FCSTD DOCUMENT  (FreeCAD 1.0R39285 (Git))
Label: ButtonLayout
License: All rights reserved
LicenseURL: https://en.wikipedia.org/wiki/All_rights_reserved
objects: Sketcher::SketchObject×7, TechDraw::DrawSVGTemplate×3, TechDraw::DrawProjGroupItem×3, TechDraw::DrawPage×3, Spreadsheet::Sheet×1, PartDesign::Body×1
note: 15 computed .brp shape members not serialized (recipe doc carries the construction recipe); baked Part::Feature solids carry a one-line shape summary decoded from their .brp

FEATURE [Sketcher::SketchObject] Sketch  label="SketchB4Rotation"
  ArcFitTolerance = 1e-06
  AttachmentSupport = -> [XY_Plane]
  FullyConstrained = true
  MakeInternals = false
  MapMode = 5
  expr: Constraints[108] = Spreadsheet.HolesEdgeStep
  expr: Constraints[112] = Spreadsheet.HolesEdgeStep
  expr: Constraints[113] = Spreadsheet.HolesEdgeStep
  expr: Constraints[120] = -Spreadsheet.ButtonsCenterOffset
  expr: Constraints[121] = Spreadsheet.ButtonsCenterOffset
  expr: Constraints[148] = Spreadsheet.HolesEdgeStep
  expr: Constraints[149] = Spreadsheet.HolesEdgeStep
  expr: Constraints[54] = Spreadsheet.BoxLength
  expr: Constraints[55] = Spreadsheet.BoxWidth
  expr: Constraints[67] = Spreadsheet.HolesEdgeStep
  expr: Constraints[68] = Spreadsheet.HolesEdgeStep
  expr: Constraints[69] = Spreadsheet.BoxLength / 2
  expr: Constraints[70] = Spreadsheet.BoxWidth / 2
  expr: Constraints[73] = Spreadsheet.Button24Outer
  expr: Constraints[75] = Spreadsheet.Button24Outer
  expr: Constraints[86] = Spreadsheet.OLEDLength
  expr: Constraints[87] = Spreadsheet.OLEDWidth
  sketch-geometry (54):
    g0: Circle CenterX=-22 CenterY=-60.3 CenterZ=0 NormalX=0 NormalY=0 NormalZ=1 AngleXU=0 Radius=15
    g1: Circle CenterX=22 CenterY=-60.3 CenterZ=0 NormalX=0 NormalY=0 NormalZ=1 AngleXU=0 Radius=15
    g2: Circle CenterX=37.5 CenterY=-24.5398 CenterZ=0 NormalX=0 NormalY=0 NormalZ=1 AngleXU=0 Radius=12
    g3: Circle CenterX=69.47 CenterY=18.8602 CenterZ=0 NormalX=0 NormalY=0 NormalZ=1 AngleXU=0 Radius=12
    g4: Circle CenterX=66.57 CenterY=-12.5998 CenterZ=0 NormalX=0 NormalY=0 NormalZ=1 AngleXU=0 Radius=12
    g5: Circle CenterX=100.97 CenterY=18.9602 CenterZ=0 NormalX=0 NormalY=0 NormalZ=1 AngleXU=0 Radius=12
    g6: Circle CenterX=131.97 CenterY=14.9602 CenterZ=0 NormalX=0 NormalY=0 NormalZ=1 AngleXU=0 Radius=12
    g7: Circle CenterX=97.92 CenterY=-12.6198 CenterZ=0 NormalX=0 NormalY=0 NormalZ=1 AngleXU=0 Radius=12
    g8: Circle CenterX=129.01 CenterY=-16.3798 CenterZ=0 NormalX=0 NormalY=0 NormalZ=1 AngleXU=0 Radius=12
    g9: Circle CenterX=-37.5 CenterY=-7 CenterZ=0 NormalX=0 NormalY=0 NormalZ=1 AngleXU=0 Radius=12
    g10: Circle CenterX=-65.5 CenterY=6.5 CenterZ=0 NormalX=0 NormalY=0 NormalZ=1 AngleXU=0 Radius=12
    g11: Circle CenterX=-96.5 CenterY=7.5 CenterZ=0 NormalX=0 NormalY=0 NormalZ=1 AngleXU=0 Radius=12
    g12: Circle CenterX=-128 CenterY=83 CenterZ=0 NormalX=0 NormalY=0 NormalZ=1 AngleXU=0 Radius=12
    g13: Circle CenterX=-95 CenterY=83 CenterZ=0 NormalX=0 NormalY=0 NormalZ=1 AngleXU=0 Radius=12
    g14: Circle CenterX=-62 CenterY=83 CenterZ=0 NormalX=0 NormalY=0 NormalZ=1 AngleXU=0 Radius=12
    g15: Circle CenterX=-29 CenterY=83 CenterZ=0 NormalX=0 NormalY=0 NormalZ=1 AngleXU=0 Radius=12
    g16: Circle CenterX=40.47 CenterY=6.50016 CenterZ=0 NormalX=0 NormalY=0 NormalZ=1 AngleXU=0 Radius=12
    g17: LineSegment StartX=114.5 StartY=92.75 StartZ=0 EndX=114.5 EndY=73.25 EndZ=0
    g18: LineSegment StartX=114.5 StartY=73.25 StartZ=0 EndX=141.5 EndY=73.25 EndZ=0
    g19: LineSegment StartX=141.5 StartY=73.25 StartZ=0 EndX=141.5 EndY=92.75 EndZ=0
    g20: LineSegment StartX=141.5 StartY=92.75 StartZ=0 EndX=114.5 EndY=92.75 EndZ=0
    g21: LineSegment StartX=-172 StartY=127 StartZ=0 EndX=-172 EndY=-127 EndZ=0
    g22: LineSegment StartX=-172 StartY=-127 StartZ=0 EndX=172 EndY=-127 EndZ=0
    g23: LineSegment StartX=172 StartY=-127 StartZ=0 EndX=172 EndY=127 EndZ=0
    g24: LineSegment StartX=172 StartY=127 StartZ=0 EndX=-172 EndY=127 EndZ=0
    g25: LineSegment StartX=-162 StartY=117 StartZ=0 EndX=-162 EndY=-117 EndZ=0
    g26: LineSegment StartX=-162 StartY=-117 StartZ=0 EndX=162 EndY=-117 EndZ=0
    g27: LineSegment StartX=162 StartY=-117 StartZ=0 EndX=162 EndY=117 EndZ=0
    g28: LineSegment StartX=162 StartY=117 StartZ=0 EndX=-162 EndY=117 EndZ=0
    g29: Circle CenterX=-152 CenterY=-107 CenterZ=0 NormalX=0 NormalY=0 NormalZ=1 AngleXU=0 Radius=2
    g30: Circle CenterX=40.47 CenterY=6.50016 CenterZ=0 NormalX=0 NormalY=0 NormalZ=1 AngleXU=0 Radius=14
    g31: Circle CenterX=69.47 CenterY=18.8602 CenterZ=0 NormalX=0 NormalY=0 NormalZ=1 AngleXU=0 Radius=14
    g32: Circle CenterX=100.97 CenterY=18.9602 CenterZ=0 NormalX=0 NormalY=0 NormalZ=1 AngleXU=0 Radius=14
    g33: Circle CenterX=131.97 CenterY=14.9602 CenterZ=0 NormalX=0 NormalY=0 NormalZ=1 AngleXU=0 Radius=14
    g34: Circle CenterX=37.5 CenterY=-24.5398 CenterZ=0 NormalX=0 NormalY=0 NormalZ=1 AngleXU=0 Radius=14
    g35: Circle CenterX=66.57 CenterY=-12.5998 CenterZ=0 NormalX=0 NormalY=0 NormalZ=1 AngleXU=0 Radius=14
    g36: Circle CenterX=97.92 CenterY=-12.6198 CenterZ=0 NormalX=0 NormalY=0 NormalZ=1 AngleXU=0 Radius=14
    g37: Circle CenterX=129.01 CenterY=-16.3798 CenterZ=0 NormalX=0 NormalY=0 NormalZ=1 AngleXU=0 Radius=14
    g38: Circle CenterX=-37.5 CenterY=-7 CenterZ=0 NormalX=0 NormalY=0 NormalZ=1 AngleXU=0 Radius=14
    g39: Circle CenterX=-65.5 CenterY=6.5 CenterZ=0 NormalX=0 NormalY=0 NormalZ=1 AngleXU=0 Radius=14
    g40: Circle CenterX=-96.5 CenterY=7.5 CenterZ=0 NormalX=0 NormalY=0 NormalZ=1 AngleXU=0 Radius=14
    g41: Circle CenterX=-128 CenterY=83 CenterZ=0 NormalX=0 NormalY=0 NormalZ=1 AngleXU=0 Radius=14
    g42: Circle CenterX=-152 CenterY=-107 CenterZ=0 NormalX=0 NormalY=0 NormalZ=1 AngleXU=0 Radius=1.5
    g43: Circle CenterX=152 CenterY=-107 CenterZ=0 NormalX=0 NormalY=0 NormalZ=1 AngleXU=0 Radius=2
    g44: Circle CenterX=152 CenterY=-107 CenterZ=0 NormalX=0 NormalY=0 NormalZ=1 AngleXU=0 Radius=1.5
    g45: Circle CenterX=-152 CenterY=107 CenterZ=0 NormalX=0 NormalY=0 NormalZ=1 AngleXU=0 Radius=2
    g46: Circle CenterX=-152 CenterY=107 CenterZ=0 NormalX=0 NormalY=0 NormalZ=1 AngleXU=0 Radius=1.5
    g47: Circle CenterX=-95 CenterY=83 CenterZ=0 NormalX=0 NormalY=0 NormalZ=1 AngleXU=0 Radius=14
    g48: Circle CenterX=-62 CenterY=83 CenterZ=0 NormalX=0 NormalY=0 NormalZ=1 AngleXU=0 Radius=14
    g49: Circle CenterX=44.47 CenterY=37.0002 CenterZ=0 NormalX=0 NormalY=0 NormalZ=1 AngleXU=0 Radius=12
    g50: Circle CenterX=44.47 CenterY=37.0002 CenterZ=0 NormalX=0 NormalY=0 NormalZ=1 AngleXU=0 Radius=14
    g51: Circle CenterX=-29 CenterY=83 CenterZ=0 NormalX=0 NormalY=0 NormalZ=1 AngleXU=0 Radius=14
    g52: Circle CenterX=152 CenterY=107 CenterZ=0 NormalX=0 NormalY=0 NormalZ=1 AngleXU=0 Radius=2
    g53: Circle CenterX=152 CenterY=107 CenterZ=0 NormalX=0 NormalY=0 NormalZ=1 AngleXU=0 Radius=1.5
  constraints (143):
    c: Equal(g2, g3-g16) x14
    c: Diameter(g2) = 24  '24mm Button'
    c: Equal(g0,g1)
    c: Diameter(g0) = 30  '30mm Button'
    c: DistanceX(g2,g16) = 2.97
    c: DistanceX(g16,g3) = 29
    c: DistanceX(g4,g3) = 2.9
    c: DistanceX(g3,g5) = 31.5
    c: DistanceX(g7,g5) = 3.05
    c: DistanceX(g8,g6) = 2.96
    c: DistanceY(g8,g6) = 31.34
    c: DistanceX(g11,g10) = 31
    c: DistanceX(g10,g9) = 28
    c: DistanceX(g5,g6) = 31
    c: DistanceX(g12,g13) = 33
    c: DistanceX(g13,g14) = 33
    c: DistanceX(g14,g15) = 33
    c: DistanceY(g2,g16) = 31.04  'LP-LK-Y'
    c: DistanceY(g4,g3) = 31.46  'MP-MK-Y'
    c: DistanceY(g9,g10) = 13.5
    c: DistanceX(g9,g0) = 15.5
    c: DistanceY(g0,g9) = 53.3
    c: Coincident(g17,g18)
    c: Coincident(g18,g19)
    c: Coincident(g19,g20)
    c: Coincident(g20,g17)
    c: Vertical(g17)
    c: Vertical(g19)
    c: Horizontal(g18)
    c: Horizontal(g20)
    c: Horizontal(g12,g13)
    c: Horizontal(g13,g14)
    c: Horizontal(g14,g15)
    c: Coincident(g21,g22)
    c: Coincident(g22,g23)
    c: Coincident(g23,g24)
    c: Coincident(g24,g21)
    c: Vertical(g21)
    c: Vertical(g23)
    c: Horizontal(g22)
    c: Horizontal(g24)
    c: DistanceX(g24,g24) = 344
    c: DistanceY(g21,g21) = 254
    c: Coincident(g25,g26)
    c: Coincident(g26,g27)
    c: Coincident(g27,g28)
    c: Coincident(g28,g25)
    c: Vertical(g25)
    c: Vertical(g27)
    c: Horizontal(g26)
    c: Horizontal(g28)
    c: DistanceY(g21,g25) = 10
    c: Distance(g25,g21) = 10
    c: Diameter(g29) = 4
    c: Distance(g29,g26) = 10
    c: Distance(g29,g25) = 10
    c: Distance(g-1,g23) = 172
    c: Distance(g-1,g22) = 127
    c: DistanceY(g7,g5) = 31.58  'HP-HK-Y'
    c: Distance(g16,g3) = 31.5241  'LP-MP-Distance'
    c: Diameter(g30) = 28
    c: Coincident(g30,g16)
    c: Diameter(g31) = 28
    c: Coincident(g31,g3)
    c: Diameter(g32) = 28
    c: Coincident(g32,g5)
    c: Diameter(g33) = 28
    c: Coincident(g33,g6)
    c: Diameter(g34) = 28
    c: Coincident(g34,g2)
    c: DistanceY(g16,g3) = 12.36
    c: Diameter(g35) = 28
    c: Coincident(g35,g4)
    c: DistanceX(g20,g20) = 27
    c: DistanceY(g19,g19) = 19.5
    c: Diameter(g36) = 28
    c: Coincident(g36,g7)
    c: Diameter(g37) = 28
    c: Coincident(g8,g37)
    c: Diameter(g38) = 28
    c: Coincident(g9,g38)
    c: Diameter(g39) = 28
    c: Coincident(g10,g39)
    c: Diameter(g40) = 28
    c: Coincident(g11,g40)
    c: Distance(g10,g9) = 31.0846  'D-R-Distance'
    c: Distance(g4,g16) = 32.3422  'LP-MK-Distance'
    c: Distance(g4,g2) = 31.4266  'LK-MK-Distance'
    c: Diameter(g41) = 28
    c: Coincident(g12,g41)
    c: Diameter(g42) = 3
    c: Coincident(g29,g42)
    c: Diameter(g43) = 4
    c: Diameter(g44) = 3
    c: Coincident(g43,g44)
    c: Distance(g44,g26) = 10
    c: Diameter(g45) = 4
    c: Diameter(g46) = 3
    c: Coincident(g45,g46)
    c: Distance(g45,g28) = 10
    c: Distance(g45,g25) = 10
    c: Distance(g25,g24) = 10
    c: Distance(g9,g22) = 120
    c: Diameter(g47) = 28
    c: Coincident(g13,g47)
    c: Diameter(g48) = 28
    c: Coincident(g14,g48)
    c: DistanceX(g-2,g9) = -37.5
    c: DistanceX(g-2,g2) = 37.5
    c: Symmetric(g1,g0,g-2)
    c: Distance(g11,g10) = 31.0161  'L-D-Distance'
    c: DistanceY(g10,g11) = 1
    c: DistanceY(g6,g5) = 4
    c: DistanceY(g10,g16) = 0.00016
    c: Equal(g49,g16)
    c: DistanceY(g16,g49) = 30.5
    c: Diameter(g50) = 28
    c: Coincident(g49,g50)
    c: DistanceX(g16,g49) = 4
    c: Diameter(g51) = 28
    c: Coincident(g15,g51)
    c: DistanceY(g3,g5) = 0.1
    c: Distance(g3,g5) = 31.5002
    c: Distance(g5,g6) = 31.257
    c: Distance(g16,g49) = 30.7612
    c: Distance(g3,g4) = 31.5934
    c: Distance(g5,g7) = 31.7269
    c: Distance(g6,g8) = 31.4795
    c: Distance(g7,g8) = 31.3165
    c: Distance(g4,g7) = 31.35
    c: Distance(g16,g2) = 31.1818
    c: Distance(g49,g3) = 30.8879
    c: Diameter(g52) = 4
    c: Diameter(g53) = 3
    c: Coincident(g52,g53)
    c: Distance(g52,g28) = 10
    c: Distance(g52,g27) = 10
    c: DistanceY(g12,g45) = 24
    c: DistanceX(g45,g12) = 24
    c: DistanceX(g19,g52) = 10.5
    c: DistanceY(g19,g52) = 14.25
    c: Distance(g43,g27) = 10
    c: Distance(g26,g23) = 10
FEATURE [Spreadsheet::Sheet] Spreadsheet
  cells = A1='Name; B1='Value; C1='Comment; A2='BoxLength; B2(BoxLength)==344 mm; A3='BoxWidth; B3(BoxWidth)==254 mm; A4='Button24; B4(Button24)==24 mm; A5='Button24Outer; B5(Button24Outer)==28 mm; A6='Button30; B6(Button30)==30 mm; A7='Button30Outer; B7(Button30Outer)==33 mm; A8='OLEDLength; B8(OLEDLength)==27 mm; A9='OLEDWidth; B9(OLEDWidth)==19.5 mm; A10='ButtonsCenterOffset; B10(ButtonsCenterOffset)==37.5 mm; A11='Button24FlapWidth; B11(Button24FlapWidth)==4.5 mm; C11='Buttons I have are snap-ins, they have clips on sides; A12='Button24FlapLength; B12(Button24FlapLength)==26.5 mm; C12='Total length of the cutout from one side to another - measured by grabbing the flaps with calipers; A13='HolesEdgeStep; B13(HolesEdgeStep)==10 mm; C13='Step from the edge of acrylic to the center of the corner hole; A14='Button30FlapWidth; B14(Button30FlapWidth)==4.75 mm; A15='Button30FlapLength; B15(Button30FlapLength)==32 mm
FEATURE [Sketcher::SketchObject] Sketch001  label="Sketch10DegInwards"
  ArcFitTolerance = 1e-06
  AttachmentSupport = -> [XY_Plane]
  FullyConstrained = false
  MakeInternals = false
  MapMode = 5
  expr: Constraints[120] = Spreadsheet.Button24FlapLength
  expr: Constraints[121] = Spreadsheet.Button24FlapLength
  expr: Constraints[122] = Spreadsheet.Button24FlapLength
  expr: Constraints[123] = Spreadsheet.Button24FlapLength / 2
  expr: Constraints[124] = Spreadsheet.Button24FlapLength / 2
  expr: Constraints[125] = Spreadsheet.Button24FlapLength / 2
  expr: Constraints[126] = Spreadsheet.Button24FlapWidth
  expr: Constraints[127] = Spreadsheet.Button24FlapWidth
  expr: Constraints[128] = Spreadsheet.Button24FlapWidth
  expr: Constraints[129] = Spreadsheet.Button24FlapWidth / 2
  expr: Constraints[130] = Spreadsheet.Button24FlapWidth / 2
  expr: Constraints[131] = Spreadsheet.Button24FlapWidth / 2
  expr: Constraints[22] = Spreadsheet.BoxLength
  expr: Constraints[23] = Spreadsheet.BoxWidth
  expr: Constraints[259] = Spreadsheet.Button24FlapLength
  expr: Constraints[260] = Spreadsheet.Button24FlapLength
  expr: Constraints[261] = Spreadsheet.Button24FlapLength
  expr: Constraints[262] = Spreadsheet.Button24FlapWidth
  expr: Constraints[275] = Spreadsheet.Button24FlapWidth / 2
  expr: Constraints[276] = Spreadsheet.Button24FlapWidth / 2
  expr: Constraints[277] = Spreadsheet.Button24FlapWidth / 2
  expr: Constraints[278] = Spreadsheet.Button24FlapWidth / 2
  expr: Constraints[279] = Spreadsheet.Button24FlapWidth / 2
  expr: Constraints[280] = Spreadsheet.Button24FlapWidth / 2
  expr: Constraints[281] = Spreadsheet.Button24FlapWidth / 2
  expr: Constraints[282] = Spreadsheet.Button24FlapWidth / 2
  expr: Constraints[283] = Spreadsheet.Button24FlapWidth / 2
  expr: Constraints[284] = Spreadsheet.Button24FlapWidth / 2
  expr: Constraints[285] = Spreadsheet.Button24FlapWidth / 2
  expr: Constraints[286] = Spreadsheet.Button24FlapWidth / 2
  expr: Constraints[287] = Spreadsheet.Button24FlapWidth / 2
  expr: Constraints[288] = Spreadsheet.Button24FlapLength / 2
  expr: Constraints[289] = Spreadsheet.Button24FlapLength
  expr: Constraints[290] = Spreadsheet.Button24FlapLength / 2
  expr: Constraints[291] = Spreadsheet.Button24FlapLength / 2
  expr: Constraints[292] = Spreadsheet.Button24FlapLength / 2
  expr: Constraints[293] = Spreadsheet.Button24FlapLength / 2
  expr: Constraints[294] = Spreadsheet.Button24FlapLength / 2
  expr: Constraints[295] = Spreadsheet.Button24FlapLength / 2
  expr: Constraints[296] = Spreadsheet.Button24FlapLength / 2
  expr: Constraints[297] = Spreadsheet.Button24FlapLength / 2
  expr: Constraints[298] = Spreadsheet.Button24FlapLength / 2
  expr: Constraints[299] = Spreadsheet.Button24FlapLength / 2
  expr: Constraints[300] = Spreadsheet.Button24FlapLength / 2
  expr: Constraints[301] = Spreadsheet.Button24FlapLength / 2
  expr: Constraints[35] = Spreadsheet.HolesEdgeStep
  expr: Constraints[36] = Spreadsheet.HolesEdgeStep
  expr: Constraints[37] = Spreadsheet.BoxLength / 2
  expr: Constraints[38] = Spreadsheet.BoxWidth / 2
  expr: Constraints[39] = Spreadsheet.OLEDLength
  expr: Constraints[409] = Spreadsheet.Button30
  expr: Constraints[40] = Spreadsheet.OLEDWidth
  expr: Constraints[427] = Spreadsheet.Button30FlapLength
  expr: Constraints[428] = Spreadsheet.Button30FlapLength / 2
  expr: Constraints[429] = Spreadsheet.Button30FlapLength / 2
  expr: Constraints[430] = Spreadsheet.Button30FlapWidth
  expr: Constraints[431] = Spreadsheet.Button30FlapWidth / 2
  expr: Constraints[432] = Spreadsheet.Button30FlapWidth / 2
  expr: Constraints[43] = Spreadsheet.HolesEdgeStep
  expr: Constraints[44] = Spreadsheet.HolesEdgeStep
  expr: Constraints[48] = Spreadsheet.HolesEdgeStep
  expr: Constraints[49] = Spreadsheet.HolesEdgeStep
  expr: Constraints[50] = Spreadsheet.HolesEdgeStep
  expr: Constraints[63] = Spreadsheet.ButtonsCenterOffset
  expr: Constraints[81] = -Spreadsheet.ButtonsCenterOffset
  sketch-geometry (160):
    g0: ArcOfCircle CenterX=-128 CenterY=83 CenterZ=0 NormalX=0 NormalY=0 NormalZ=1 AngleXU=0 Radius=12 StartAngle=3.33021 EndAngle=6.09457
    g1: ArcOfCircle CenterX=-95 CenterY=83 CenterZ=0 NormalX=0 NormalY=0 NormalZ=1 AngleXU=0 Radius=12 StartAngle=3.33021 EndAngle=6.09457
    g2: ArcOfCircle CenterX=-62 CenterY=83 CenterZ=0 NormalX=0 NormalY=0 NormalZ=1 AngleXU=0 Radius=12 StartAngle=3.33021 EndAngle=6.09457
    g3: ArcOfCircle CenterX=-29 CenterY=83 CenterZ=0 NormalX=0 NormalY=0 NormalZ=1 AngleXU=0 Radius=12 StartAngle=3.33021 EndAngle=6.09457
    g4: LineSegment StartX=114.5 StartY=92.75 StartZ=0 EndX=114.5 EndY=73.25 EndZ=0
    g5: LineSegment StartX=114.5 StartY=73.25 StartZ=0 EndX=141.5 EndY=73.25 EndZ=0
    g6: LineSegment StartX=141.5 StartY=73.25 StartZ=0 EndX=141.5 EndY=92.75 EndZ=0
    g7: LineSegment StartX=141.5 StartY=92.75 StartZ=0 EndX=114.5 EndY=92.75 EndZ=0
    g8: LineSegment StartX=-172 StartY=127 StartZ=0 EndX=-172 EndY=-127 EndZ=0
    g9: LineSegment StartX=-172 StartY=-127 StartZ=0 EndX=172 EndY=-127 EndZ=0
    g10: LineSegment StartX=172 StartY=-127 StartZ=0 EndX=172 EndY=127 EndZ=0
    g11: LineSegment StartX=172 StartY=127 StartZ=0 EndX=-172 EndY=127 EndZ=0
    g12: LineSegment StartX=-162 StartY=117 StartZ=0 EndX=-162 EndY=-117 EndZ=0
    g13: LineSegment StartX=-162 StartY=-117 StartZ=0 EndX=162 EndY=-117 EndZ=0
    g14: LineSegment StartX=162 StartY=-117 StartZ=0 EndX=162 EndY=117 EndZ=0
    g15: LineSegment StartX=162 StartY=117 StartZ=0 EndX=-162 EndY=117 EndZ=0
    g16: Circle CenterX=-152 CenterY=-107 CenterZ=0 NormalX=0 NormalY=0 NormalZ=1 AngleXU=0 Radius=2
    g17: Circle CenterX=152 CenterY=-107 CenterZ=0 NormalX=0 NormalY=0 NormalZ=1 AngleXU=0 Radius=2
    g18: Circle CenterX=-152 CenterY=107 CenterZ=0 NormalX=0 NormalY=0 NormalZ=1 AngleXU=0 Radius=2
    g19: Circle CenterX=152 CenterY=107 CenterZ=0 NormalX=0 NormalY=0 NormalZ=1 AngleXU=0 Radius=2
    g20: ArcOfCircle CenterX=-37.5 CenterY=-5.11795 CenterZ=0 NormalX=0 NormalY=0 NormalZ=1 AngleXU=0 Radius=12 StartAngle=3.33021 EndAngle=6.09457
    g21: ArcOfCircle CenterX=-62.72 CenterY=13.0402 CenterZ=0 NormalX=0 NormalY=0 NormalZ=1 AngleXU=0 Radius=12 StartAngle=3.33021 EndAngle=6.09457
    g22: ArcOfCircle CenterX=-93.08 CenterY=19.4093 CenterZ=0 NormalX=0 NormalY=0 NormalZ=1 AngleXU=0 Radius=12 StartAngle=3.33021 EndAngle=6.09457
    g23: ArcOfCircle CenterX=37.5 CenterY=-22.3921 CenterZ=0 NormalX=0 NormalY=0 NormalZ=1 AngleXU=0 Radius=12 StartAngle=3.33021 EndAngle=6.09457
    g24: ArcOfCircle CenterX=61.45 CenterY=25.8987 CenterZ=0 NormalX=0 NormalY=0 NormalZ=1 AngleXU=0 Radius=12 StartAngle=3.33021 EndAngle=6.09457
    g25: ArcOfCircle CenterX=64.06 CenterY=-5.58705 CenterZ=0 NormalX=0 NormalY=0 NormalZ=1 AngleXU=0 Radius=12 StartAngle=3.33021 EndAngle=6.09457
    g26: ArcOfCircle CenterX=92.46 CenterY=31.4654 CenterZ=0 NormalX=0 NormalY=0 NormalZ=1 AngleXU=0 Radius=12 StartAngle=3.33021 EndAngle=6.09457
    g27: ArcOfCircle CenterX=123.68 CenterY=32.9074 CenterZ=0 NormalX=0 NormalY=0 NormalZ=1 AngleXU=0 Radius=12 StartAngle=3.33021 EndAngle=6.09457
    g28: ArcOfCircle CenterX=94.93 CenterY=-0.164634 CenterZ=0 NormalX=0 NormalY=0 NormalZ=1 AngleXU=0 Radius=12 StartAngle=3.33021 EndAngle=6.09457
    g29: ArcOfCircle CenterX=126.2 CenterY=1.52943 CenterZ=0 NormalX=0 NormalY=0 NormalZ=1 AngleXU=0 Radius=12 StartAngle=3.33021 EndAngle=6.09457
    g30: ArcOfCircle CenterX=35.04 CenterY=8.69222 CenterZ=0 NormalX=0 NormalY=0 NormalZ=1 AngleXU=0 Radius=12 StartAngle=0.188616 EndAngle=2.95298
    g31: ArcOfCircle CenterX=33.68 CenterY=39.4235 CenterZ=0 NormalX=0 NormalY=0 NormalZ=1 AngleXU=0 Radius=12 StartAngle=3.33021 EndAngle=6.09457
    g32: LineSegment StartX=-106.33 StartY=21.6593 StartZ=0 EndX=-106.33 EndY=17.1593 EndZ=0
    g33: LineSegment StartX=-106.33 StartY=17.1593 StartZ=0 EndX=-104.867 EndY=17.1593 EndZ=0
    g34: LineSegment StartX=-79.83 StartY=17.1593 StartZ=0 EndX=-79.83 EndY=21.6593 EndZ=0
    g35: LineSegment StartX=-79.83 StartY=21.6593 StartZ=0 EndX=-81.2928 EndY=21.6593 EndZ=0
    g36: LineSegment StartX=-75.97 StartY=15.2902 StartZ=0 EndX=-75.97 EndY=10.7902 EndZ=0
    g37: LineSegment StartX=-75.97 StartY=10.7902 StartZ=0 EndX=-74.5072 EndY=10.7902 EndZ=0
    g38: LineSegment StartX=-49.47 StartY=10.7902 StartZ=0 EndX=-49.47 EndY=15.2902 EndZ=0
    g39: LineSegment StartX=-49.47 StartY=15.2902 StartZ=0 EndX=-50.9328 EndY=15.2902 EndZ=0
    g40: LineSegment StartX=-50.75 StartY=-2.86795 StartZ=0 EndX=-50.75 EndY=-7.36795 EndZ=0
    g41: LineSegment StartX=-50.75 StartY=-7.36795 StartZ=0 EndX=-49.2872 EndY=-7.36795 EndZ=0
    g42: LineSegment StartX=-24.25 StartY=-7.36795 StartZ=0 EndX=-24.25 EndY=-2.86795 EndZ=0
    g43: LineSegment StartX=-24.25 StartY=-2.86795 StartZ=0 EndX=-25.7128 EndY=-2.86795 EndZ=0
    g44: LineSegment StartX=-104.867 StartY=21.6593 StartZ=0 EndX=-106.33 EndY=21.6593 EndZ=0
    g45: LineSegment StartX=-81.2928 StartY=17.1593 StartZ=0 EndX=-79.83 EndY=17.1593 EndZ=0
    g46: ArcOfCircle CenterX=-93.08 CenterY=19.4093 CenterZ=0 NormalX=0 NormalY=0 NormalZ=1 AngleXU=0 Radius=12 StartAngle=0.188616 EndAngle=2.95298
    g47: ArcOfCircle CenterX=-62.72 CenterY=13.0402 CenterZ=0 NormalX=0 NormalY=0 NormalZ=1 AngleXU=0 Radius=12 StartAngle=0.188616 EndAngle=2.95298
    g48: LineSegment StartX=-74.5072 StartY=15.2902 StartZ=0 EndX=-75.97 EndY=15.2902 EndZ=0
    g49: LineSegment StartX=-50.9328 StartY=10.7902 StartZ=0 EndX=-49.47 EndY=10.7902 EndZ=0
    g50: LineSegment StartX=-49.2872 StartY=-2.86795 StartZ=0 EndX=-50.75 EndY=-2.86795 EndZ=0
    g51: LineSegment StartX=-25.7128 StartY=-7.36795 StartZ=0 EndX=-24.25 EndY=-7.36795 EndZ=0
    g52: ArcOfCircle CenterX=-37.5 CenterY=-5.11795 CenterZ=0 NormalX=0 NormalY=0 NormalZ=1 AngleXU=0 Radius=12 StartAngle=0.188616 EndAngle=2.95298
    g53: LineSegment StartX=20.43 StartY=41.6735 StartZ=0 EndX=20.43 EndY=37.1735 EndZ=0
    g54: LineSegment StartX=20.43 StartY=37.1735 StartZ=0 EndX=21.8928 EndY=37.1735 EndZ=0
    g55: LineSegment StartX=46.93 StartY=37.1735 StartZ=0 EndX=46.93 EndY=41.6735 EndZ=0
    g56: LineSegment StartX=46.93 StartY=41.6735 StartZ=0 EndX=45.4672 EndY=41.6735 EndZ=0
    g57: LineSegment StartX=21.79 StartY=10.9422 StartZ=0 EndX=21.79 EndY=6.44222 EndZ=0
    g58: LineSegment StartX=21.79 StartY=6.44222 StartZ=0 EndX=23.2528 EndY=6.44222 EndZ=0
    g59: LineSegment StartX=48.29 StartY=6.44222 StartZ=0 EndX=48.29 EndY=10.9422 EndZ=0
    g60: LineSegment StartX=48.29 StartY=10.9422 StartZ=0 EndX=46.8272 EndY=10.9422 EndZ=0
    g61: LineSegment StartX=24.25 StartY=-20.1421 StartZ=0 EndX=24.25 EndY=-24.6421 EndZ=0
    g62: LineSegment StartX=24.25 StartY=-24.6421 StartZ=0 EndX=25.7128 EndY=-24.6421 EndZ=0
    g63: LineSegment StartX=50.75 StartY=-24.6421 StartZ=0 EndX=50.75 EndY=-20.1421 EndZ=0
    g64: LineSegment StartX=50.75 StartY=-20.1421 StartZ=0 EndX=49.2872 EndY=-20.1421 EndZ=0
    g65: LineSegment StartX=50.81 StartY=-3.33705 StartZ=0 EndX=50.81 EndY=-7.83705 EndZ=0
    g66: LineSegment StartX=50.81 StartY=-7.83705 StartZ=0 EndX=52.2728 EndY=-7.83705 EndZ=0
    g67: LineSegment StartX=77.31 StartY=-7.83705 StartZ=0 EndX=77.31 EndY=-3.33705 EndZ=0
    g68: LineSegment StartX=77.31 StartY=-3.33705 StartZ=0 EndX=75.8472 EndY=-3.33705 EndZ=0
    g69: LineSegment StartX=48.2 StartY=28.1487 StartZ=0 EndX=48.2 EndY=23.6487 EndZ=0
    g70: LineSegment StartX=48.2 StartY=23.6487 StartZ=0 EndX=49.6628 EndY=23.6487 EndZ=0
    g71: LineSegment StartX=74.7 StartY=23.6487 StartZ=0 EndX=74.7 EndY=28.1487 EndZ=0
    g72: LineSegment StartX=74.7 StartY=28.1487 StartZ=0 EndX=73.2372 EndY=28.1487 EndZ=0
    g73: LineSegment StartX=79.21 StartY=33.7154 StartZ=0 EndX=79.21 EndY=29.2154 EndZ=0
    g74: LineSegment StartX=79.21 StartY=29.2154 StartZ=0 EndX=80.6728 EndY=29.2154 EndZ=0
    g75: LineSegment StartX=105.71 StartY=29.2154 StartZ=0 EndX=105.71 EndY=33.7154 EndZ=0
    g76: LineSegment StartX=105.71 StartY=33.7154 StartZ=0 EndX=104.247 EndY=33.7154 EndZ=0
    g77: LineSegment StartX=110.43 StartY=35.1574 StartZ=0 EndX=110.43 EndY=30.6574 EndZ=0
    g78: LineSegment StartX=110.43 StartY=30.6574 StartZ=0 EndX=111.893 EndY=30.6574 EndZ=0
    g79: LineSegment StartX=136.93 StartY=30.6574 StartZ=0 EndX=136.93 EndY=35.1574 EndZ=0
    g80: LineSegment StartX=136.93 StartY=35.1574 StartZ=0 EndX=135.467 EndY=35.1574 EndZ=0
    g81: LineSegment StartX=81.68 StartY=2.08537 StartZ=0 EndX=81.68 EndY=-2.41463 EndZ=0
    g82: LineSegment StartX=81.68 StartY=-2.41463 StartZ=0 EndX=83.1428 EndY=-2.41463 EndZ=0
    g83: LineSegment StartX=108.18 StartY=-2.41463 StartZ=0 EndX=108.18 EndY=2.08537 EndZ=0
    g84: LineSegment StartX=108.18 StartY=2.08537 StartZ=0 EndX=106.717 EndY=2.08537 EndZ=0
    g85: LineSegment StartX=112.95 StartY=3.77943 StartZ=0 EndX=112.95 EndY=-0.720574 EndZ=0
    g86: LineSegment StartX=112.95 StartY=-0.720574 StartZ=0 EndX=114.413 EndY=-0.720574 EndZ=0
    g87: LineSegment StartX=139.45 StartY=-0.720574 StartZ=0 EndX=139.45 EndY=3.77943 EndZ=0
    g88: LineSegment StartX=139.45 StartY=3.77943 StartZ=0 EndX=137.987 EndY=3.77943 EndZ=0
    g89: LineSegment StartX=-141.25 StartY=85.25 StartZ=0 EndX=-141.25 EndY=80.75 EndZ=0
    g90: LineSegment StartX=-141.25 StartY=80.75 StartZ=0 EndX=-139.787 EndY=80.75 EndZ=0
    g91: LineSegment StartX=-114.75 StartY=80.75 StartZ=0 EndX=-114.75 EndY=85.25 EndZ=0
    g92: LineSegment StartX=-114.75 StartY=85.25 StartZ=0 EndX=-116.213 EndY=85.25 EndZ=0
    g93: LineSegment StartX=-108.25 StartY=85.25 StartZ=0 EndX=-108.25 EndY=80.75 EndZ=0
    g94: LineSegment StartX=-108.25 StartY=80.75 StartZ=0 EndX=-106.787 EndY=80.75 EndZ=0
    g95: LineSegment StartX=-81.75 StartY=80.75 StartZ=0 EndX=-81.75 EndY=85.25 EndZ=0
    g96: LineSegment StartX=-81.75 StartY=85.25 StartZ=0 EndX=-83.2128 EndY=85.25 EndZ=0
    g97: LineSegment StartX=-75.25 StartY=85.25 StartZ=0 EndX=-75.25 EndY=80.75 EndZ=0
    g98: LineSegment StartX=-75.25 StartY=80.75 StartZ=0 EndX=-73.7872 EndY=80.75 EndZ=0
    g99: LineSegment StartX=-48.75 StartY=80.75 StartZ=0 EndX=-48.75 EndY=85.25 EndZ=0
    g100: LineSegment StartX=-48.75 StartY=85.25 StartZ=0 EndX=-50.2128 EndY=85.25 EndZ=0
    g101: LineSegment StartX=-42.25 StartY=85.25 StartZ=0 EndX=-42.25 EndY=80.75 EndZ=0
    g102: LineSegment StartX=-42.25 StartY=80.75 StartZ=0 EndX=-40.7872 EndY=80.75 EndZ=0
    g103: LineSegment StartX=-15.75 StartY=80.75 StartZ=0 EndX=-15.75 EndY=85.25 EndZ=0
    g104: LineSegment StartX=-15.75 StartY=85.25 StartZ=0 EndX=-17.2128 EndY=85.25 EndZ=0
    g105: LineSegment StartX=-139.787 StartY=85.25 StartZ=0 EndX=-141.25 EndY=85.25 EndZ=0
    g106: LineSegment StartX=-116.213 StartY=80.75 StartZ=0 EndX=-114.75 EndY=80.75 EndZ=0
    g107: ArcOfCircle CenterX=-128 CenterY=83 CenterZ=0 NormalX=0 NormalY=0 NormalZ=1 AngleXU=0 Radius=12 StartAngle=0.188616 EndAngle=2.95298
    g108: LineSegment StartX=-106.787 StartY=85.25 StartZ=0 EndX=-108.25 EndY=85.25 EndZ=0
    g109: LineSegment StartX=-83.2128 StartY=80.75 StartZ=0 EndX=-81.75 EndY=80.75 EndZ=0
    g110: ArcOfCircle CenterX=-95 CenterY=83 CenterZ=0 NormalX=0 NormalY=0 NormalZ=1 AngleXU=0 Radius=12 StartAngle=0.188616 EndAngle=2.95298
    g111: LineSegment StartX=-73.7872 StartY=85.25 StartZ=0 EndX=-75.25 EndY=85.25 EndZ=0
    g112: LineSegment StartX=-50.2128 StartY=80.75 StartZ=0 EndX=-48.75 EndY=80.75 EndZ=0
    g113: ArcOfCircle CenterX=-62 CenterY=83 CenterZ=0 NormalX=0 NormalY=0 NormalZ=1 AngleXU=0 Radius=12 StartAngle=0.188616 EndAngle=2.95298
    g114: LineSegment StartX=-40.7872 StartY=85.25 StartZ=0 EndX=-42.25 EndY=85.25 EndZ=0
    g115: LineSegment StartX=-17.2128 StartY=80.75 StartZ=0 EndX=-15.75 EndY=80.75 EndZ=0
    g116: ArcOfCircle CenterX=-29 CenterY=83 CenterZ=0 NormalX=0 NormalY=0 NormalZ=1 AngleXU=0 Radius=12 StartAngle=0.188616 EndAngle=2.95298
    g117: ArcOfCircle CenterX=33.68 CenterY=39.4235 CenterZ=0 NormalX=0 NormalY=0 NormalZ=1 AngleXU=0 Radius=12 StartAngle=0.188616 EndAngle=2.95298
    g118: LineSegment StartX=21.8928 StartY=41.6735 StartZ=0 EndX=20.43 EndY=41.6735 EndZ=0
    g119: LineSegment StartX=45.4672 StartY=37.1735 StartZ=0 EndX=46.93 EndY=37.1735 EndZ=0
    g120: LineSegment StartX=49.6628 StartY=28.1487 StartZ=0 EndX=48.2 EndY=28.1487 EndZ=0
    g121: LineSegment StartX=73.2372 StartY=23.6487 StartZ=0 EndX=74.7 EndY=23.6487 EndZ=0
    g122: ArcOfCircle CenterX=61.45 CenterY=25.8987 CenterZ=0 NormalX=0 NormalY=0 NormalZ=1 AngleXU=0 Radius=12 StartAngle=0.188616 EndAngle=2.95298
    g123: LineSegment StartX=80.6728 StartY=33.7154 StartZ=0 EndX=79.21 EndY=33.7154 EndZ=0
    g124: LineSegment StartX=104.247 StartY=29.2154 StartZ=0 EndX=105.71 EndY=29.2154 EndZ=0
    g125: ArcOfCircle CenterX=92.46 CenterY=31.4654 CenterZ=0 NormalX=0 NormalY=0 NormalZ=1 AngleXU=0 Radius=12 StartAngle=0.188616 EndAngle=2.95298
    g126: LineSegment StartX=111.893 StartY=35.1574 StartZ=0 EndX=110.43 EndY=35.1574 EndZ=0
    g127: LineSegment StartX=135.467 StartY=30.6574 StartZ=0 EndX=136.93 EndY=30.6574 EndZ=0
    g128: ArcOfCircle CenterX=123.68 CenterY=32.9074 CenterZ=0 NormalX=0 NormalY=0 NormalZ=1 AngleXU=0 Radius=12 StartAngle=0.188616 EndAngle=2.95298
    g129: ArcOfCircle CenterX=35.04 CenterY=8.69222 CenterZ=0 NormalX=0 NormalY=0 NormalZ=1 AngleXU=0 Radius=12 StartAngle=3.33021 EndAngle=6.09457
    g130: LineSegment StartX=23.2528 StartY=10.9422 StartZ=0 EndX=21.79 EndY=10.9422 EndZ=0
    g131: LineSegment StartX=46.8272 StartY=6.44222 StartZ=0 EndX=48.29 EndY=6.44222 EndZ=0
    g132: LineSegment StartX=25.7128 StartY=-20.1421 StartZ=0 EndX=24.25 EndY=-20.1421 EndZ=0
    g133: LineSegment StartX=49.2872 StartY=-24.6421 StartZ=0 EndX=50.75 EndY=-24.6421 EndZ=0
    g134: ArcOfCircle CenterX=37.5 CenterY=-22.3921 CenterZ=0 NormalX=0 NormalY=0 NormalZ=1 AngleXU=0 Radius=12 StartAngle=0.188616 EndAngle=2.95298
    g135: ArcOfCircle CenterX=64.06 CenterY=-5.58705 CenterZ=0 NormalX=0 NormalY=0 NormalZ=1 AngleXU=0 Radius=12 StartAngle=0.188616 EndAngle=2.95298
    g136: LineSegment StartX=52.2728 StartY=-3.33705 StartZ=0 EndX=50.81 EndY=-3.33705 EndZ=0
    g137: LineSegment StartX=75.8472 StartY=-7.83705 StartZ=0 EndX=77.31 EndY=-7.83705 EndZ=0
    g138: LineSegment StartX=83.1428 StartY=2.08537 StartZ=0 EndX=81.68 EndY=2.08537 EndZ=0
    g139: ArcOfCircle CenterX=94.93 CenterY=-0.164634 CenterZ=0 NormalX=0 NormalY=0 NormalZ=1 AngleXU=0 Radius=12 StartAngle=0.188616 EndAngle=2.95298
    g140: LineSegment StartX=106.717 StartY=-2.41463 StartZ=0 EndX=108.18 EndY=-2.41463 EndZ=0
    g141: LineSegment StartX=114.413 StartY=3.77943 StartZ=0 EndX=112.95 EndY=3.77943 EndZ=0
    g142: LineSegment StartX=137.987 StartY=-0.720574 StartZ=0 EndX=139.45 EndY=-0.720574 EndZ=0
    g143: ArcOfCircle CenterX=126.2 CenterY=1.52943 CenterZ=0 NormalX=0 NormalY=0 NormalZ=1 AngleXU=0 Radius=12 StartAngle=0.188616 EndAngle=2.95298
    g144: ArcOfCircle CenterX=28.44 CenterY=-60.3 CenterZ=0 NormalX=0 NormalY=0 NormalZ=1 AngleXU=0 Radius=15 StartAngle=3.3006 EndAngle=6.12418
    g145: ArcOfCircle CenterX=-31.49 CenterY=-60.3 CenterZ=0 NormalX=0 NormalY=0 NormalZ=1 AngleXU=0 Radius=15 StartAngle=3.3006 EndAngle=6.12418
    g146: LineSegment StartX=-47.49 StartY=-57.925 StartZ=0 EndX=-47.49 EndY=-62.675 EndZ=0
    g147: LineSegment StartX=-47.49 StartY=-62.675 StartZ=0 EndX=-46.3008 EndY=-62.675 EndZ=0
    g148: LineSegment StartX=-15.49 StartY=-62.675 StartZ=0 EndX=-15.49 EndY=-57.925 EndZ=0
    g149: LineSegment StartX=-15.49 StartY=-57.925 StartZ=0 EndX=-16.6792 EndY=-57.925 EndZ=0
    g150: LineSegment StartX=12.44 StartY=-57.925 StartZ=0 EndX=12.44 EndY=-62.675 EndZ=0
    g151: LineSegment StartX=12.44 StartY=-62.675 StartZ=0 EndX=13.6292 EndY=-62.675 EndZ=0
    g152: LineSegment StartX=44.44 StartY=-62.675 StartZ=0 EndX=44.44 EndY=-57.925 EndZ=0
    g153: LineSegment StartX=44.44 StartY=-57.925 StartZ=0 EndX=43.2508 EndY=-57.925 EndZ=0
    g154: LineSegment StartX=-46.3008 StartY=-57.925 StartZ=0 EndX=-47.49 EndY=-57.925 EndZ=0
    g155: ArcOfCircle CenterX=-31.49 CenterY=-60.3 CenterZ=0 NormalX=0 NormalY=0 NormalZ=1 AngleXU=0 Radius=15 StartAngle=0.159002 EndAngle=2.98259
    g156: LineSegment StartX=-16.6792 StartY=-62.675 StartZ=0 EndX=-15.49 EndY=-62.675 EndZ=0
    g157: LineSegment StartX=13.6292 StartY=-57.925 StartZ=0 EndX=12.44 EndY=-57.925 EndZ=0
    g158: LineSegment StartX=43.2508 StartY=-62.675 StartZ=0 EndX=44.44 EndY=-62.675 EndZ=0
    g159: ArcOfCircle CenterX=28.44 CenterY=-60.3 CenterZ=0 NormalX=0 NormalY=0 NormalZ=1 AngleXU=0 Radius=15 StartAngle=0.159002 EndAngle=2.98259
  constraints (445):
    c: DistanceX(g0,g1) = 33
    c: DistanceX(g1,g2) = 33
    c: DistanceX(g2,g3) = 33
    c: Coincident(g4,g5)
    c: Coincident(g5,g6)
    c: Coincident(g6,g7)
    c: Coincident(g7,g4)
    c: Vertical(g4)
    c: Vertical(g6)
    c: Horizontal(g5)
    c: Horizontal(g7)
    c: Horizontal(g0,g1)
    c: Horizontal(g1,g2)
    c: Horizontal(g2,g3)
    c: Coincident(g8,g9)
    c: Coincident(g9,g10)
    c: Coincident(g10,g11)
    c: Coincident(g11,g8)
    c: Vertical(g8)
    c: Vertical(g10)
    c: Horizontal(g9)
    c: Horizontal(g11)
    c: DistanceX(g11,g11) = 344
    c: DistanceY(g8,g8) = 254
    c: Coincident(g12,g13)
    c: Coincident(g13,g14)
    c: Coincident(g14,g15)
    c: Coincident(g15,g12)
    c: Vertical(g12)
    c: Vertical(g14)
    c: Horizontal(g13)
    c: Horizontal(g15)
    c: DistanceY(g8,g12) = 10
    c: Distance(g12,g8) = 10
    c: Diameter(g16) = 4
    c: Distance(g16,g13) = 10
    c: Distance(g16,g12) = 10
    c: Distance(g-1,g10) = 172
    c: Distance(g-1,g9) = 127
    c: DistanceX(g7,g7) = 27
    c: DistanceY(g6,g6) = 19.5
    c: Diameter(g17) = 4
    c: Diameter(g18) = 4
    c: Distance(g18,g15) = 10
    c: Distance(g18,g12) = 10
    c: Distance(g13,g10) = 10
    c: Distance(g12,g11) = 10
    c: Diameter(g19) = 4
    c: Distance(g19,g15) = 10
    c: Distance(g19,g14) = 10
    c: Distance(g17,g14) = 10
    c: Equal(g23, g24-g30) x7
    c: Diameter(g23) = 24
    c: Equal(g31,g30)
    c: DistanceY(g22) = 19.4093
    c: DistanceY(g21) = 13.0402
    c: DistanceY(g20) = -5.11795
    c: DistanceX(g23) = 37.5
    c: DistanceY(g23) = -22.3921
    c: DistanceY(g30) = 8.69222
    c: DistanceY(g31) = 39.4235
    c: Equal(g0,g1)
    c: Equal(g1,g2)
    c: Equal(g2,g3)
    c: Equal(g0,g20)
    c: Equal(g20,g21)
    c: Equal(g21,g22)
    c: Equal(g22,g31)
    c: DistanceY(g24) = 25.8987
    c: DistanceY(g26) = 31.4654
    c: DistanceY(g28) = -0.164634
    c: DistanceY(g29) = 1.52943
    c: DistanceY(g27) = 32.9074
    c: DistanceX(g22,g21) = 30.36
    c: DistanceX(g21,g20) = 25.22
    c: DistanceX(g-2,g20) = -37.5
    c: DistanceY(g25) = -5.58705
    c: DistanceX(g23,g25) = 26.56
    c: DistanceX(g30,g23) = 2.46
    c: DistanceX(g31,g23) = 3.82
    c: DistanceX(g23,g24) = 23.95
    c: DistanceX(g23,g28) = 57.43
    c: DistanceX(g23,g26) = 54.96
    c: DistanceX(g23,g29) = 88.7
    c: DistanceX(g23,g27) = 86.18
    c: Distance(g17,g13) = 10
    c: DistanceY(g6,g19) = 14.25
    c: DistanceX(g6,g19) = 10.5
    c: DistanceY(g0,g18) = 24
    c: DistanceX(g18,g0) = 24
    c: Coincident(g32,g33)
    c: Coincident(g45,g34)
    c: Coincident(g34,g35)
    c: Coincident(g44,g32)
    c: Vertical(g32)
    c: Vertical(g34)
    c: Horizontal(g33)
    c: Horizontal(g35)
    c: Coincident(g36,g37)
    c: Coincident(g49,g38)
    c: Coincident(g38,g39)
    c: Coincident(g48,g36)
    c: Vertical(g36)
    c: Vertical(g38)
    c: Horizontal(g37)
    c: Horizontal(g39)
    c: Coincident(g40,g41)
    c: Coincident(g51,g42)
    c: Coincident(g42,g43)
    c: Coincident(g50,g40)
    c: Vertical(g40)
    c: Vertical(g42)
    c: Horizontal(g41)
    c: Horizontal(g43)
    c: DistanceX(g44,g35) = 26.5
    c: DistanceX(g48,g39) = 26.5
    c: DistanceX(g50,g43) = 26.5
    c: Distance(g22,g34) = 13.25
    c: Distance(g21,g38) = 13.25
    c: Distance(g20,g42) = 13.25
    c: DistanceY(g32,g32) = 4.5
    c: DistanceY(g36,g36) = 4.5
    c: DistanceY(g40,g40) = 4.5
    c: Distance(g22,g33) = 2.25
    c: Distance(g21,g37) = 2.25
    c: Distance(g20,g41) = 2.25
    c: PointOnObject(g46,g44)
    c: PointOnObject(g35,g46)
    c: PointOnObject(g44,g46)
    c: Coincident(g33,g22)
    c: Equal(g22,g46)
    c: Coincident(g22,g45)
    c: PointOnObject(g46,g35)
    c: Coincident(g22,g46)
    c: PointOnObject(g47,g48)
    c: Equal(g21,g47)
    c: PointOnObject(g21,g49)
    c: Coincident(g21,g47)
    c: Coincident(g39,g47)
    c: PointOnObject(g48,g47)
    c: Coincident(g37,g21)
    c: PointOnObject(g49,g21)
    c: PointOnObject(g43,g52)
    c: Coincident(g52,g50)
    c: Coincident(g20,g41)
    c: Equal(g20,g52)
    c: Coincident(g20,g51)
    c: PointOnObject(g52,g43)
    c: Coincident(g20,g52)
    c: Coincident(g53,g54)
    c: Coincident(g119,g55)
    c: Coincident(g55,g56)
    c: Coincident(g118,g53)
    c: Vertical(g53)
    c: Vertical(g55)
    c: Horizontal(g54)
    c: Horizontal(g56)
    c: Coincident(g57,g58)
    c: Coincident(g131,g59)
    c: Coincident(g59,g60)
    c: Coincident(g130,g57)
    c: Vertical(g57)
    c: Vertical(g59)
    c: Horizontal(g58)
    c: Horizontal(g60)
    c: Coincident(g61,g62)
    c: Coincident(g133,g63)
    c: Coincident(g63,g64)
    c: Coincident(g132,g61)
    c: Vertical(g61)
    c: Vertical(g63)
    c: Horizontal(g62)
    c: Horizontal(g64)
    c: Coincident(g65,g66)
    c: Coincident(g137,g67)
    c: Coincident(g67,g68)
    c: Coincident(g136,g65)
    c: Vertical(g65)
    c: Vertical(g67)
    c: Horizontal(g66)
    c: Horizontal(g68)
    c: Coincident(g69,g70)
    c: Coincident(g121,g71)
    c: Coincident(g71,g72)
    c: Coincident(g120,g69)
    c: Vertical(g69)
    c: Vertical(g71)
    c: Horizontal(g70)
    c: Horizontal(g72)
    c: Coincident(g73,g74)
    c: Coincident(g124,g75)
    c: Coincident(g75,g76)
    c: Coincident(g123,g73)
    c: Vertical(g73)
    c: Vertical(g75)
    c: Horizontal(g74)
    c: Horizontal(g76)
    c: Coincident(g77,g78)
    c: Coincident(g127,g79)
    c: Coincident(g79,g80)
    c: Coincident(g126,g77)
    c: Vertical(g77)
    c: Vertical(g79)
    c: Horizontal(g78)
    c: Horizontal(g80)
    c: Coincident(g81,g82)
    c: Coincident(g140,g83)
    c: Coincident(g83,g84)
    c: Coincident(g138,g81)
    c: Vertical(g81)
    c: Vertical(g83)
    c: Horizontal(g82)
    c: Horizontal(g84)
    c: Coincident(g85,g86)
    c: Coincident(g142,g87)
    c: Coincident(g87,g88)
    c: Coincident(g141,g85)
    c: Vertical(g85)
    c: Vertical(g87)
    c: Horizontal(g86)
    c: Horizontal(g88)
    c: Coincident(g89,g90)
    c: Coincident(g106,g91)
    c: Coincident(g91,g92)
    c: Coincident(g105,g89)
    c: Vertical(g89)
    c: Vertical(g91)
    c: Horizontal(g90)
    c: Horizontal(g92)
    c: Coincident(g93,g94)
    c: Coincident(g109,g95)
    c: Coincident(g95,g96)
    c: Coincident(g108,g93)
    c: Vertical(g93)
    c: Vertical(g95)
    c: Horizontal(g94)
    c: Horizontal(g96)
    c: Coincident(g97,g98)
    c: Coincident(g112,g99)
    c: Coincident(g99,g100)
    c: Coincident(g111,g97)
    c: Vertical(g97)
    c: Vertical(g99)
    c: Horizontal(g98)
    c: Horizontal(g100)
    c: Coincident(g101,g102)
    c: Coincident(g115,g103)
    c: Coincident(g103,g104)
    c: Coincident(g114,g101)
    c: Vertical(g101)
    c: Vertical(g103)
    c: Horizontal(g102)
    c: Horizontal(g104)
    c: DistanceX(g132,g64) = 26.5
    c: DistanceX(g130,g60) = 26.5
    c: DistanceX(g118,g56) = 26.5
    c: DistanceY(g89,g89) = 4.5
    c: Equal(g89,g93)
    c: Equal(g93,g97)
    c: Equal(g97,g101)
    c: Equal(g101,g53)
    c: Equal(g53,g57)
    c: Equal(g57,g61)
    c: Equal(g61,g65)
    c: Equal(g65,g69)
    c: Equal(g69,g73)
    c: Equal(g73,g81)
    c: Equal(g81,g77)
    c: Equal(g77,g85)
    c: Distance(g0,g92) = 2.25
    c: Distance(g1,g96) = 2.25
    c: Distance(g2,g100) = 2.25
    c: Distance(g3,g104) = 2.25
    c: Distance(g31,g56) = 2.25
    c: Distance(g30,g60) = 2.25
    c: Distance(g23,g64) = 2.25
    c: Distance(g25,g68) = 2.25
    c: Distance(g24,g72) = 2.25
    c: Distance(g26,g76) = 2.25
    c: Distance(g28,g84) = 2.25
    c: Distance(g27,g80) = 2.25
    c: Distance(g29,g88) = 2.25
    c: Distance(g0,g91) = 13.25
    c: DistanceX(g105,g92) = 26.5
    c: Distance(g1,g95) = 13.25
    c: Distance(g2,g99) = 13.25
    c: Distance(g3,g103) = 13.25
    c: Distance(g31,g55) = 13.25
    c: Distance(g30,g59) = 13.25
    c: Distance(g23,g63) = 13.25
    c: Distance(g24,g71) = 13.25
    c: Distance(g25,g67) = 13.25
    c: Distance(g28,g83) = 13.25
    c: Distance(g26,g75) = 13.25
    c: Distance(g27,g79) = 13.25
    c: Distance(g29,g87) = 13.25
    c: PointOnObject(g107,g105)
    c: PointOnObject(g92,g107)
    c: PointOnObject(g105,g107)
    c: Coincident(g90,g0)
    c: Equal(g0,g107)
    c: Coincident(g0,g106)
    c: PointOnObject(g107,g92)
    c: Coincident(g0,g107)
    c: PointOnObject(g110,g108)
    c: PointOnObject(g96,g110)
    c: PointOnObject(g108,g110)
    c: Coincident(g94,g1)
    c: Equal(g1,g110)
    c: Coincident(g1,g109)
    c: PointOnObject(g110,g96)
    c: Coincident(g1,g110)
    c: PointOnObject(g113,g111)
    c: PointOnObject(g100,g113)
    c: PointOnObject(g111,g113)
    c: Coincident(g98,g2)
    c: Equal(g2,g113)
    c: Coincident(g2,g112)
    c: PointOnObject(g113,g100)
    c: Coincident(g2,g113)
    c: PointOnObject(g116,g114)
    c: PointOnObject(g104,g116)
    c: PointOnObject(g114,g116)
    c: Coincident(g102,g3)
    c: Equal(g3,g116)
    c: Coincident(g3,g115)
    c: PointOnObject(g116,g104)
    c: Coincident(g3,g116)
    c: PointOnObject(g117,g118)
    c: Equal(g31,g117)
    c: PointOnObject(g31,g119)
    c: Coincident(g31,g117)
    c: Coincident(g56,g117)
    c: PointOnObject(g118,g117)
    c: Coincident(g54,g31)
    c: PointOnObject(g119,g31)
    c: PointOnObject(g122,g120)
    c: PointOnObject(g72,g122)
    c: PointOnObject(g120,g122)
    c: Coincident(g70,g24)
    c: Equal(g24,g122)
    c: Coincident(g24,g121)
    c: PointOnObject(g122,g72)
    c: Coincident(g24,g122)
    c: PointOnObject(g76,g125)
    c: Coincident(g125,g123)
    c: Coincident(g74,g26)
    c: Equal(g26,g125)
    c: Coincident(g26,g124)
    c: PointOnObject(g125,g76)
    c: Coincident(g26,g125)
    c: PointOnObject(g80,g128)
    c: Coincident(g128,g126)
    c: Coincident(g78,g27)
    c: Equal(g27,g128)
    c: Coincident(g27,g127)
    c: PointOnObject(g128,g80)
    c: Coincident(g27,g128)
    c: PointOnObject(g129,g131)
    c: Equal(g30,g129)
    c: PointOnObject(g30,g130)
    c: Coincident(g30,g129)
    c: Coincident(g60,g30)
    c: PointOnObject(g130,g30)
    c: Coincident(g58,g129)
    c: PointOnObject(g131,g129)
    c: PointOnObject(g134,g132)
    c: PointOnObject(g64,g134)
    c: PointOnObject(g132,g134)
    c: Coincident(g62,g23)
    c: Equal(g23,g134)
    c: Coincident(g23,g133)
    c: PointOnObject(g134,g64)
    c: Coincident(g23,g134)
    c: PointOnObject(g135,g136)
    c: Equal(g25,g135)
    c: PointOnObject(g25,g137)
    c: Coincident(g25,g135)
    c: Coincident(g68,g135)
    c: PointOnObject(g136,g135)
    c: Coincident(g66,g25)
    c: PointOnObject(g137,g25)
    c: PointOnObject(g139,g138)
    c: PointOnObject(g84,g139)
    c: PointOnObject(g138,g139)
    c: Equal(g28,g139)
    c: PointOnObject(g28,g140)
    c: PointOnObject(g139,g84)
    c: Coincident(g28,g139)
    c: Coincident(g82,g28)
    c: PointOnObject(g140,g28)
    c: PointOnObject(g143,g141)
    c: PointOnObject(g88,g143)
    c: PointOnObject(g141,g143)
    c: Coincident(g86,g29)
    c: Equal(g29,g143)
    c: Coincident(g29,g142)
    c: PointOnObject(g143,g88)
    c: Coincident(g29,g143)
    c: DistanceX(g145) = -31.49
    c: DistanceY(g145) = -60.3
    c: DistanceX(g144) = 28.44
    c: DistanceY(g144) = -60.3
    c: Diameter(g145) = 30
    c: Equal(g145,g144)
    c: Coincident(g146,g147)
    c: Coincident(g156,g148)
    c: Coincident(g148,g149)
    c: Coincident(g154,g146)
    c: Vertical(g146)
    c: Vertical(g148)
    c: Horizontal(g147)
    c: Horizontal(g149)
    c: Coincident(g150,g151)
    c: Coincident(g158,g152)
    c: Coincident(g152,g153)
    c: Coincident(g157,g150)
    c: Vertical(g150)
    c: Vertical(g152)
    c: Horizontal(g151)
    c: Horizontal(g153)
    c: DistanceX(g154,g149) = 32
    c: Distance(g145,g148) = 16
    c: Distance(g144,g152) = 16
    c: DistanceY(g146,g146) = 4.75
    c: Distance(g145,g147) = 2.375
    c: Distance(g144,g151) = 2.375
    c: Equal(g148,g150)
    c: PointOnObject(g155,g154)
    c: PointOnObject(g149,g155)
    c: PointOnObject(g154,g155)
    c: Equal(g145,g155)
    c: PointOnObject(g145,g156)
    c: PointOnObject(g155,g149)
    c: Coincident(g145,g155)
    c: Coincident(g147,g145)
    c: PointOnObject(g156,g145)
    c: PointOnObject(g159,g157)
    c: PointOnObject(g153,g159)
    c: PointOnObject(g157,g144)
    c: Coincident(g151,g144)
    c: Equal(g144,g159)
    c: Coincident(g144,g158)
    c: PointOnObject(g159,g153)
    c: Coincident(g144,g159)
FEATURE [Sketcher::SketchObject] Sketch002  label="Sketch10DegInwards001"
  ArcFitTolerance = 1e-06
  AttachmentSupport = -> [XY_Plane]
  FullyConstrained = false
  MakeInternals = false
  MapMode = 5
  expr: Constraints[100] = Spreadsheet.Button24FlapLength
  expr: Constraints[101] = Spreadsheet.Button24FlapLength
  expr: Constraints[102] = Spreadsheet.Button24FlapLength
  expr: Constraints[103] = Spreadsheet.Button24FlapLength / 2
  expr: Constraints[104] = Spreadsheet.Button24FlapLength / 2
  expr: Constraints[105] = Spreadsheet.Button24FlapLength / 2
  expr: Constraints[106] = Spreadsheet.Button24FlapWidth
  expr: Constraints[107] = Spreadsheet.Button24FlapWidth
  expr: Constraints[108] = Spreadsheet.Button24FlapWidth
  expr: Constraints[109] = Spreadsheet.Button24FlapWidth / 2
  expr: Constraints[110] = Spreadsheet.Button24FlapWidth / 2
  expr: Constraints[111] = Spreadsheet.Button24FlapWidth / 2
  expr: Constraints[22] = Spreadsheet.BoxLength
  expr: Constraints[239] = Spreadsheet.Button24FlapLength
  expr: Constraints[23] = Spreadsheet.BoxWidth
  expr: Constraints[240] = Spreadsheet.Button24FlapLength
  expr: Constraints[241] = Spreadsheet.Button24FlapLength
  expr: Constraints[242] = Spreadsheet.Button24FlapWidth
  expr: Constraints[255] = Spreadsheet.Button24FlapWidth / 2
  expr: Constraints[256] = Spreadsheet.Button24FlapWidth / 2
  expr: Constraints[257] = Spreadsheet.Button24FlapWidth / 2
  expr: Constraints[258] = Spreadsheet.Button24FlapWidth / 2
  expr: Constraints[259] = Spreadsheet.Button24FlapWidth / 2
  expr: Constraints[25] = Spreadsheet.BoxLength / 2
  expr: Constraints[260] = Spreadsheet.Button24FlapWidth / 2
  expr: Constraints[261] = Spreadsheet.Button24FlapWidth / 2
  expr: Constraints[262] = Spreadsheet.Button24FlapWidth / 2
  expr: Constraints[263] = Spreadsheet.Button24FlapWidth / 2
  expr: Constraints[264] = Spreadsheet.Button24FlapWidth / 2
  expr: Constraints[265] = Spreadsheet.Button24FlapWidth / 2
  expr: Constraints[266] = Spreadsheet.Button24FlapWidth / 2
  expr: Constraints[267] = Spreadsheet.Button24FlapWidth / 2
  expr: Constraints[268] = Spreadsheet.Button24FlapLength / 2
  expr: Constraints[269] = Spreadsheet.Button24FlapLength
  expr: Constraints[26] = Spreadsheet.BoxWidth / 2
  expr: Constraints[270] = Spreadsheet.Button24FlapLength / 2
  expr: Constraints[271] = Spreadsheet.Button24FlapLength / 2
  expr: Constraints[272] = Spreadsheet.Button24FlapLength / 2
  expr: Constraints[273] = Spreadsheet.Button24FlapLength / 2
  expr: Constraints[274] = Spreadsheet.Button24FlapLength / 2
  expr: Constraints[275] = Spreadsheet.Button24FlapLength / 2
  expr: Constraints[276] = Spreadsheet.Button24FlapLength / 2
  expr: Constraints[277] = Spreadsheet.Button24FlapLength / 2
  expr: Constraints[278] = Spreadsheet.Button24FlapLength / 2
  expr: Constraints[279] = Spreadsheet.Button24FlapLength / 2
  expr: Constraints[27] = Spreadsheet.OLEDLength
  expr: Constraints[280] = Spreadsheet.Button24FlapLength / 2
  expr: Constraints[281] = Spreadsheet.Button24FlapLength / 2
  expr: Constraints[28] = Spreadsheet.OLEDWidth
  expr: Constraints[389] = Spreadsheet.Button30
  expr: Constraints[407] = Spreadsheet.Button30FlapLength
  expr: Constraints[408] = Spreadsheet.Button30FlapLength / 2
  expr: Constraints[409] = Spreadsheet.Button30FlapLength / 2
  expr: Constraints[410] = Spreadsheet.Button30FlapWidth
  expr: Constraints[411] = Spreadsheet.Button30FlapWidth / 2
  expr: Constraints[412] = Spreadsheet.Button30FlapWidth / 2
  expr: Constraints[44] = Spreadsheet.ButtonsCenterOffset
  expr: Constraints[62] = -Spreadsheet.ButtonsCenterOffset
  sketch-geometry (156):
    g0: ArcOfCircle CenterX=-128 CenterY=83 CenterZ=0 NormalX=0 NormalY=0 NormalZ=1 AngleXU=0 Radius=12 StartAngle=3.33021 EndAngle=6.09457
    g1: ArcOfCircle CenterX=-95 CenterY=83 CenterZ=0 NormalX=0 NormalY=0 NormalZ=1 AngleXU=0 Radius=12 StartAngle=3.33021 EndAngle=6.09457
    g2: ArcOfCircle CenterX=-62 CenterY=83 CenterZ=0 NormalX=0 NormalY=0 NormalZ=1 AngleXU=0 Radius=12 StartAngle=3.33021 EndAngle=6.09457
    g3: ArcOfCircle CenterX=-29 CenterY=83 CenterZ=0 NormalX=0 NormalY=0 NormalZ=1 AngleXU=0 Radius=12 StartAngle=3.33021 EndAngle=6.09457
    g4: LineSegment StartX=114.5 StartY=92.75 StartZ=0 EndX=114.5 EndY=73.25 EndZ=0
    g5: LineSegment StartX=114.5 StartY=73.25 StartZ=0 EndX=141.5 EndY=73.25 EndZ=0
    g6: LineSegment StartX=141.5 StartY=73.25 StartZ=0 EndX=141.5 EndY=92.75 EndZ=0
    g7: LineSegment StartX=141.5 StartY=92.75 StartZ=0 EndX=114.5 EndY=92.75 EndZ=0
    g8: LineSegment StartX=-172 StartY=127 StartZ=0 EndX=-172 EndY=-127 EndZ=0
    g9: LineSegment StartX=-172 StartY=-127 StartZ=0 EndX=172 EndY=-127 EndZ=0
    g10: LineSegment StartX=172 StartY=-127 StartZ=0 EndX=172 EndY=127 EndZ=0
    g11: LineSegment StartX=172 StartY=127 StartZ=0 EndX=-172 EndY=127 EndZ=0
    g12: Circle CenterX=-152 CenterY=-107 CenterZ=0 NormalX=0 NormalY=0 NormalZ=1 AngleXU=0 Radius=2
    g13: Circle CenterX=152 CenterY=-107 CenterZ=0 NormalX=0 NormalY=0 NormalZ=1 AngleXU=0 Radius=2
    g14: Circle CenterX=-152 CenterY=107 CenterZ=0 NormalX=0 NormalY=0 NormalZ=1 AngleXU=0 Radius=2
    g15: Circle CenterX=152 CenterY=107 CenterZ=0 NormalX=0 NormalY=0 NormalZ=1 AngleXU=0 Radius=2
    g16: ArcOfCircle CenterX=-37.5 CenterY=-5.11795 CenterZ=0 NormalX=0 NormalY=0 NormalZ=1 AngleXU=0 Radius=12 StartAngle=3.33021 EndAngle=6.09457
    g17: ArcOfCircle CenterX=-62.72 CenterY=13.0402 CenterZ=0 NormalX=0 NormalY=0 NormalZ=1 AngleXU=0 Radius=12 StartAngle=3.33021 EndAngle=6.09457
    g18: ArcOfCircle CenterX=-93.08 CenterY=19.4093 CenterZ=0 NormalX=0 NormalY=0 NormalZ=1 AngleXU=0 Radius=12 StartAngle=3.33021 EndAngle=6.09457
    g19: ArcOfCircle CenterX=37.5 CenterY=-22.3921 CenterZ=0 NormalX=0 NormalY=0 NormalZ=1 AngleXU=0 Radius=12 StartAngle=3.33021 EndAngle=6.09457
    g20: ArcOfCircle CenterX=61.45 CenterY=25.8987 CenterZ=0 NormalX=0 NormalY=0 NormalZ=1 AngleXU=0 Radius=12 StartAngle=3.33021 EndAngle=6.09457
    g21: ArcOfCircle CenterX=64.06 CenterY=-5.58705 CenterZ=0 NormalX=0 NormalY=0 NormalZ=1 AngleXU=0 Radius=12 StartAngle=3.33021 EndAngle=6.09457
    g22: ArcOfCircle CenterX=92.46 CenterY=31.4654 CenterZ=0 NormalX=0 NormalY=0 NormalZ=1 AngleXU=0 Radius=12 StartAngle=3.33021 EndAngle=6.09457
    g23: ArcOfCircle CenterX=123.68 CenterY=32.9074 CenterZ=0 NormalX=0 NormalY=0 NormalZ=1 AngleXU=0 Radius=12 StartAngle=3.33021 EndAngle=6.09457
    g24: ArcOfCircle CenterX=94.93 CenterY=-0.164634 CenterZ=0 NormalX=0 NormalY=0 NormalZ=1 AngleXU=0 Radius=12 StartAngle=3.33021 EndAngle=6.09457
    g25: ArcOfCircle CenterX=126.2 CenterY=1.52943 CenterZ=0 NormalX=0 NormalY=0 NormalZ=1 AngleXU=0 Radius=12 StartAngle=3.33021 EndAngle=6.09457
    g26: ArcOfCircle CenterX=35.04 CenterY=8.69222 CenterZ=0 NormalX=0 NormalY=0 NormalZ=1 AngleXU=0 Radius=12 StartAngle=0.188616 EndAngle=2.95298
    g27: ArcOfCircle CenterX=33.68 CenterY=39.4235 CenterZ=0 NormalX=0 NormalY=0 NormalZ=1 AngleXU=0 Radius=12 StartAngle=3.33021 EndAngle=6.09457
    g28: LineSegment StartX=-106.33 StartY=21.6593 StartZ=0 EndX=-106.33 EndY=17.1593 EndZ=0
    g29: LineSegment StartX=-106.33 StartY=17.1593 StartZ=0 EndX=-104.867 EndY=17.1593 EndZ=0
    g30: LineSegment StartX=-79.83 StartY=17.1593 StartZ=0 EndX=-79.83 EndY=21.6593 EndZ=0
    g31: LineSegment StartX=-79.83 StartY=21.6593 StartZ=0 EndX=-81.2928 EndY=21.6593 EndZ=0
    g32: LineSegment StartX=-75.97 StartY=15.2902 StartZ=0 EndX=-75.97 EndY=10.7902 EndZ=0
    g33: LineSegment StartX=-75.97 StartY=10.7902 StartZ=0 EndX=-74.5072 EndY=10.7902 EndZ=0
    g34: LineSegment StartX=-49.47 StartY=10.7902 StartZ=0 EndX=-49.47 EndY=15.2902 EndZ=0
    g35: LineSegment StartX=-49.47 StartY=15.2902 StartZ=0 EndX=-50.9328 EndY=15.2902 EndZ=0
    g36: LineSegment StartX=-50.75 StartY=-2.86795 StartZ=0 EndX=-50.75 EndY=-7.36795 EndZ=0
    g37: LineSegment StartX=-50.75 StartY=-7.36795 StartZ=0 EndX=-49.2872 EndY=-7.36795 EndZ=0
    g38: LineSegment StartX=-24.25 StartY=-7.36795 StartZ=0 EndX=-24.25 EndY=-2.86795 EndZ=0
    g39: LineSegment StartX=-24.25 StartY=-2.86795 StartZ=0 EndX=-25.7128 EndY=-2.86795 EndZ=0
    g40: LineSegment StartX=-104.867 StartY=21.6593 StartZ=0 EndX=-106.33 EndY=21.6593 EndZ=0
    g41: LineSegment StartX=-81.2928 StartY=17.1593 StartZ=0 EndX=-79.83 EndY=17.1593 EndZ=0
    g42: ArcOfCircle CenterX=-93.08 CenterY=19.4093 CenterZ=0 NormalX=0 NormalY=0 NormalZ=1 AngleXU=0 Radius=12 StartAngle=0.188616 EndAngle=2.95298
    g43: ArcOfCircle CenterX=-62.72 CenterY=13.0402 CenterZ=0 NormalX=0 NormalY=0 NormalZ=1 AngleXU=0 Radius=12 StartAngle=0.188616 EndAngle=2.95298
    g44: LineSegment StartX=-74.5072 StartY=15.2902 StartZ=0 EndX=-75.97 EndY=15.2902 EndZ=0
    g45: LineSegment StartX=-50.9328 StartY=10.7902 StartZ=0 EndX=-49.47 EndY=10.7902 EndZ=0
    g46: LineSegment StartX=-49.2872 StartY=-2.86795 StartZ=0 EndX=-50.75 EndY=-2.86795 EndZ=0
    g47: LineSegment StartX=-25.7128 StartY=-7.36795 StartZ=0 EndX=-24.25 EndY=-7.36795 EndZ=0
    g48: ArcOfCircle CenterX=-37.5 CenterY=-5.11795 CenterZ=0 NormalX=0 NormalY=0 NormalZ=1 AngleXU=0 Radius=12 StartAngle=0.188616 EndAngle=2.95298
    g49: LineSegment StartX=20.43 StartY=41.6735 StartZ=0 EndX=20.43 EndY=37.1735 EndZ=0
    g50: LineSegment StartX=20.43 StartY=37.1735 StartZ=0 EndX=21.8928 EndY=37.1735 EndZ=0
    g51: LineSegment StartX=46.93 StartY=37.1735 StartZ=0 EndX=46.93 EndY=41.6735 EndZ=0
    g52: LineSegment StartX=46.93 StartY=41.6735 StartZ=0 EndX=45.4672 EndY=41.6735 EndZ=0
    g53: LineSegment StartX=21.79 StartY=10.9422 StartZ=0 EndX=21.79 EndY=6.44222 EndZ=0
    g54: LineSegment StartX=21.79 StartY=6.44222 StartZ=0 EndX=23.2528 EndY=6.44222 EndZ=0
    g55: LineSegment StartX=48.29 StartY=6.44222 StartZ=0 EndX=48.29 EndY=10.9422 EndZ=0
    g56: LineSegment StartX=48.29 StartY=10.9422 StartZ=0 EndX=46.8272 EndY=10.9422 EndZ=0
    g57: LineSegment StartX=24.25 StartY=-20.1421 StartZ=0 EndX=24.25 EndY=-24.6421 EndZ=0
    g58: LineSegment StartX=24.25 StartY=-24.6421 StartZ=0 EndX=25.7128 EndY=-24.6421 EndZ=0
    g59: LineSegment StartX=50.75 StartY=-24.6421 StartZ=0 EndX=50.75 EndY=-20.1421 EndZ=0
    g60: LineSegment StartX=50.75 StartY=-20.1421 StartZ=0 EndX=49.2872 EndY=-20.1421 EndZ=0
    g61: LineSegment StartX=50.81 StartY=-3.33705 StartZ=0 EndX=50.81 EndY=-7.83705 EndZ=0
    g62: LineSegment StartX=50.81 StartY=-7.83705 StartZ=0 EndX=52.2728 EndY=-7.83705 EndZ=0
    g63: LineSegment StartX=77.31 StartY=-7.83705 StartZ=0 EndX=77.31 EndY=-3.33705 EndZ=0
    g64: LineSegment StartX=77.31 StartY=-3.33705 StartZ=0 EndX=75.8472 EndY=-3.33705 EndZ=0
    g65: LineSegment StartX=48.2 StartY=28.1487 StartZ=0 EndX=48.2 EndY=23.6487 EndZ=0
    g66: LineSegment StartX=48.2 StartY=23.6487 StartZ=0 EndX=49.6628 EndY=23.6487 EndZ=0
    g67: LineSegment StartX=74.7 StartY=23.6487 StartZ=0 EndX=74.7 EndY=28.1487 EndZ=0
    g68: LineSegment StartX=74.7 StartY=28.1487 StartZ=0 EndX=73.2372 EndY=28.1487 EndZ=0
    g69: LineSegment StartX=79.21 StartY=33.7154 StartZ=0 EndX=79.21 EndY=29.2154 EndZ=0
    g70: LineSegment StartX=79.21 StartY=29.2154 StartZ=0 EndX=80.6728 EndY=29.2154 EndZ=0
    g71: LineSegment StartX=105.71 StartY=29.2154 StartZ=0 EndX=105.71 EndY=33.7154 EndZ=0
    g72: LineSegment StartX=105.71 StartY=33.7154 StartZ=0 EndX=104.247 EndY=33.7154 EndZ=0
    g73: LineSegment StartX=110.43 StartY=35.1574 StartZ=0 EndX=110.43 EndY=30.6574 EndZ=0
    g74: LineSegment StartX=110.43 StartY=30.6574 StartZ=0 EndX=111.893 EndY=30.6574 EndZ=0
    g75: LineSegment StartX=136.93 StartY=30.6574 StartZ=0 EndX=136.93 EndY=35.1574 EndZ=0
    g76: LineSegment StartX=136.93 StartY=35.1574 StartZ=0 EndX=135.467 EndY=35.1574 EndZ=0
    g77: LineSegment StartX=81.68 StartY=2.08537 StartZ=0 EndX=81.68 EndY=-2.41463 EndZ=0
    g78: LineSegment StartX=81.68 StartY=-2.41463 StartZ=0 EndX=83.1428 EndY=-2.41463 EndZ=0
    g79: LineSegment StartX=108.18 StartY=-2.41463 StartZ=0 EndX=108.18 EndY=2.08537 EndZ=0
    g80: LineSegment StartX=108.18 StartY=2.08537 StartZ=0 EndX=106.717 EndY=2.08537 EndZ=0
    g81: LineSegment StartX=112.95 StartY=3.77943 StartZ=0 EndX=112.95 EndY=-0.720574 EndZ=0
    g82: LineSegment StartX=112.95 StartY=-0.720574 StartZ=0 EndX=114.413 EndY=-0.720574 EndZ=0
    g83: LineSegment StartX=139.45 StartY=-0.720574 StartZ=0 EndX=139.45 EndY=3.77943 EndZ=0
    g84: LineSegment StartX=139.45 StartY=3.77943 StartZ=0 EndX=137.987 EndY=3.77943 EndZ=0
    g85: LineSegment StartX=-141.25 StartY=85.25 StartZ=0 EndX=-141.25 EndY=80.75 EndZ=0
    g86: LineSegment StartX=-141.25 StartY=80.75 StartZ=0 EndX=-139.787 EndY=80.75 EndZ=0
    g87: LineSegment StartX=-114.75 StartY=80.75 StartZ=0 EndX=-114.75 EndY=85.25 EndZ=0
    g88: LineSegment StartX=-114.75 StartY=85.25 StartZ=0 EndX=-116.213 EndY=85.25 EndZ=0
    g89: LineSegment StartX=-108.25 StartY=85.25 StartZ=0 EndX=-108.25 EndY=80.75 EndZ=0
    g90: LineSegment StartX=-108.25 StartY=80.75 StartZ=0 EndX=-106.787 EndY=80.75 EndZ=0
    g91: LineSegment StartX=-81.75 StartY=80.75 StartZ=0 EndX=-81.75 EndY=85.25 EndZ=0
    g92: LineSegment StartX=-81.75 StartY=85.25 StartZ=0 EndX=-83.2128 EndY=85.25 EndZ=0
    g93: LineSegment StartX=-75.25 StartY=85.25 StartZ=0 EndX=-75.25 EndY=80.75 EndZ=0
    g94: LineSegment StartX=-75.25 StartY=80.75 StartZ=0 EndX=-73.7872 EndY=80.75 EndZ=0
    g95: LineSegment StartX=-48.75 StartY=80.75 StartZ=0 EndX=-48.75 EndY=85.25 EndZ=0
    g96: LineSegment StartX=-48.75 StartY=85.25 StartZ=0 EndX=-50.2128 EndY=85.25 EndZ=0
    g97: LineSegment StartX=-42.25 StartY=85.25 StartZ=0 EndX=-42.25 EndY=80.75 EndZ=0
    g98: LineSegment StartX=-42.25 StartY=80.75 StartZ=0 EndX=-40.7872 EndY=80.75 EndZ=0
    g99: LineSegment StartX=-15.75 StartY=80.75 StartZ=0 EndX=-15.75 EndY=85.25 EndZ=0
    g100: LineSegment StartX=-15.75 StartY=85.25 StartZ=0 EndX=-17.2128 EndY=85.25 EndZ=0
    g101: LineSegment StartX=-139.787 StartY=85.25 StartZ=0 EndX=-141.25 EndY=85.25 EndZ=0
    g102: LineSegment StartX=-116.213 StartY=80.75 StartZ=0 EndX=-114.75 EndY=80.75 EndZ=0
    g103: ArcOfCircle CenterX=-128 CenterY=83 CenterZ=0 NormalX=0 NormalY=0 NormalZ=1 AngleXU=0 Radius=12 StartAngle=0.188616 EndAngle=2.95298
    g104: LineSegment StartX=-106.787 StartY=85.25 StartZ=0 EndX=-108.25 EndY=85.25 EndZ=0
    g105: LineSegment StartX=-83.2128 StartY=80.75 StartZ=0 EndX=-81.75 EndY=80.75 EndZ=0
    g106: ArcOfCircle CenterX=-95 CenterY=83 CenterZ=0 NormalX=0 NormalY=0 NormalZ=1 AngleXU=0 Radius=12 StartAngle=0.188616 EndAngle=2.95298
    g107: LineSegment StartX=-73.7872 StartY=85.25 StartZ=0 EndX=-75.25 EndY=85.25 EndZ=0
    g108: LineSegment StartX=-50.2128 StartY=80.75 StartZ=0 EndX=-48.75 EndY=80.75 EndZ=0
    g109: ArcOfCircle CenterX=-62 CenterY=83 CenterZ=0 NormalX=0 NormalY=0 NormalZ=1 AngleXU=0 Radius=12 StartAngle=0.188616 EndAngle=2.95298
    g110: LineSegment StartX=-40.7872 StartY=85.25 StartZ=0 EndX=-42.25 EndY=85.25 EndZ=0
    g111: LineSegment StartX=-17.2128 StartY=80.75 StartZ=0 EndX=-15.75 EndY=80.75 EndZ=0
    g112: ArcOfCircle CenterX=-29 CenterY=83 CenterZ=0 NormalX=0 NormalY=0 NormalZ=1 AngleXU=0 Radius=12 StartAngle=0.188616 EndAngle=2.95298
    g113: ArcOfCircle CenterX=33.68 CenterY=39.4235 CenterZ=0 NormalX=0 NormalY=0 NormalZ=1 AngleXU=0 Radius=12 StartAngle=0.188616 EndAngle=2.95298
    g114: LineSegment StartX=21.8928 StartY=41.6735 StartZ=0 EndX=20.43 EndY=41.6735 EndZ=0
    g115: LineSegment StartX=45.4672 StartY=37.1735 StartZ=0 EndX=46.93 EndY=37.1735 EndZ=0
    g116: LineSegment StartX=49.6628 StartY=28.1487 StartZ=0 EndX=48.2 EndY=28.1487 EndZ=0
    g117: LineSegment StartX=73.2372 StartY=23.6487 StartZ=0 EndX=74.7 EndY=23.6487 EndZ=0
    g118: ArcOfCircle CenterX=61.45 CenterY=25.8987 CenterZ=0 NormalX=0 NormalY=0 NormalZ=1 AngleXU=0 Radius=12 StartAngle=0.188616 EndAngle=2.95298
    g119: LineSegment StartX=80.6728 StartY=33.7154 StartZ=0 EndX=79.21 EndY=33.7154 EndZ=0
    g120: LineSegment StartX=104.247 StartY=29.2154 StartZ=0 EndX=105.71 EndY=29.2154 EndZ=0
    g121: ArcOfCircle CenterX=92.46 CenterY=31.4654 CenterZ=0 NormalX=0 NormalY=0 NormalZ=1 AngleXU=0 Radius=12 StartAngle=0.188616 EndAngle=2.95298
    g122: LineSegment StartX=111.893 StartY=35.1574 StartZ=0 EndX=110.43 EndY=35.1574 EndZ=0
    g123: LineSegment StartX=135.467 StartY=30.6574 StartZ=0 EndX=136.93 EndY=30.6574 EndZ=0
    g124: ArcOfCircle CenterX=123.68 CenterY=32.9074 CenterZ=0 NormalX=0 NormalY=0 NormalZ=1 AngleXU=0 Radius=12 StartAngle=0.188616 EndAngle=2.95298
    g125: ArcOfCircle CenterX=35.04 CenterY=8.69222 CenterZ=0 NormalX=0 NormalY=0 NormalZ=1 AngleXU=0 Radius=12 StartAngle=3.33021 EndAngle=6.09457
    g126: LineSegment StartX=23.2528 StartY=10.9422 StartZ=0 EndX=21.79 EndY=10.9422 EndZ=0
    g127: LineSegment StartX=46.8272 StartY=6.44222 StartZ=0 EndX=48.29 EndY=6.44222 EndZ=0
    g128: LineSegment StartX=25.7128 StartY=-20.1421 StartZ=0 EndX=24.25 EndY=-20.1421 EndZ=0
    g129: LineSegment StartX=49.2872 StartY=-24.6421 StartZ=0 EndX=50.75 EndY=-24.6421 EndZ=0
    g130: ArcOfCircle CenterX=37.5 CenterY=-22.3921 CenterZ=0 NormalX=0 NormalY=0 NormalZ=1 AngleXU=0 Radius=12 StartAngle=0.188616 EndAngle=2.95298
    g131: ArcOfCircle CenterX=64.06 CenterY=-5.58705 CenterZ=0 NormalX=0 NormalY=0 NormalZ=1 AngleXU=0 Radius=12 StartAngle=0.188616 EndAngle=2.95298
    g132: LineSegment StartX=52.2728 StartY=-3.33705 StartZ=0 EndX=50.81 EndY=-3.33705 EndZ=0
    g133: LineSegment StartX=75.8472 StartY=-7.83705 StartZ=0 EndX=77.31 EndY=-7.83705 EndZ=0
    g134: LineSegment StartX=83.1428 StartY=2.08537 StartZ=0 EndX=81.68 EndY=2.08537 EndZ=0
    g135: ArcOfCircle CenterX=94.93 CenterY=-0.164634 CenterZ=0 NormalX=0 NormalY=0 NormalZ=1 AngleXU=0 Radius=12 StartAngle=0.188616 EndAngle=2.95298
    g136: LineSegment StartX=106.717 StartY=-2.41463 StartZ=0 EndX=108.18 EndY=-2.41463 EndZ=0
    g137: LineSegment StartX=114.413 StartY=3.77943 StartZ=0 EndX=112.95 EndY=3.77943 EndZ=0
    g138: LineSegment StartX=137.987 StartY=-0.720574 StartZ=0 EndX=139.45 EndY=-0.720574 EndZ=0
    g139: ArcOfCircle CenterX=126.2 CenterY=1.52943 CenterZ=0 NormalX=0 NormalY=0 NormalZ=1 AngleXU=0 Radius=12 StartAngle=0.188616 EndAngle=2.95298
    g140: ArcOfCircle CenterX=28.44 CenterY=-60.3 CenterZ=0 NormalX=0 NormalY=0 NormalZ=1 AngleXU=0 Radius=15 StartAngle=3.3006 EndAngle=6.12418
    g141: ArcOfCircle CenterX=-31.49 CenterY=-60.3 CenterZ=0 NormalX=0 NormalY=0 NormalZ=1 AngleXU=0 Radius=15 StartAngle=3.3006 EndAngle=6.12418
    g142: LineSegment StartX=-47.49 StartY=-57.925 StartZ=0 EndX=-47.49 EndY=-62.675 EndZ=0
    g143: LineSegment StartX=-47.49 StartY=-62.675 StartZ=0 EndX=-46.3008 EndY=-62.675 EndZ=0
    g144: LineSegment StartX=-15.49 StartY=-62.675 StartZ=0 EndX=-15.49 EndY=-57.925 EndZ=0
    g145: LineSegment StartX=-15.49 StartY=-57.925 StartZ=0 EndX=-16.6792 EndY=-57.925 EndZ=0
    g146: LineSegment StartX=12.44 StartY=-57.925 StartZ=0 EndX=12.44 EndY=-62.675 EndZ=0
    g147: LineSegment StartX=12.44 StartY=-62.675 StartZ=0 EndX=13.6292 EndY=-62.675 EndZ=0
    g148: LineSegment StartX=44.44 StartY=-62.675 StartZ=0 EndX=44.44 EndY=-57.925 EndZ=0
    g149: LineSegment StartX=44.44 StartY=-57.925 StartZ=0 EndX=43.2508 EndY=-57.925 EndZ=0
    g150: LineSegment StartX=-46.3008 StartY=-57.925 StartZ=0 EndX=-47.49 EndY=-57.925 EndZ=0
    g151: ArcOfCircle CenterX=-31.49 CenterY=-60.3 CenterZ=0 NormalX=0 NormalY=0 NormalZ=1 AngleXU=0 Radius=15 StartAngle=0.159002 EndAngle=2.98259
    g152: LineSegment StartX=-16.6792 StartY=-62.675 StartZ=0 EndX=-15.49 EndY=-62.675 EndZ=0
    g153: LineSegment StartX=13.6292 StartY=-57.925 StartZ=0 EndX=12.44 EndY=-57.925 EndZ=0
    g154: LineSegment StartX=43.2508 StartY=-62.675 StartZ=0 EndX=44.44 EndY=-62.675 EndZ=0
    g155: ArcOfCircle CenterX=28.44 CenterY=-60.3 CenterZ=0 NormalX=0 NormalY=0 NormalZ=1 AngleXU=0 Radius=15 StartAngle=0.159002 EndAngle=2.98259
  constraints (425):
    c: DistanceX(g0,g1) = 33
    c: DistanceX(g1,g2) = 33
    c: DistanceX(g2,g3) = 33
    c: Coincident(g4,g5)
    c: Coincident(g5,g6)
    c: Coincident(g6,g7)
    c: Coincident(g7,g4)
    c: Vertical(g4)
    c: Vertical(g6)
    c: Horizontal(g5)
    c: Horizontal(g7)
    c: Horizontal(g0,g1)
    c: Horizontal(g1,g2)
    c: Horizontal(g2,g3)
    c: Coincident(g8,g9)
    c: Coincident(g9,g10)
    c: Coincident(g10,g11)
    c: Coincident(g11,g8)
    c: Vertical(g8)
    c: Vertical(g10)
    c: Horizontal(g9)
    c: Horizontal(g11)
    c: DistanceX(g11,g11) = 344
    c: DistanceY(g8,g8) = 254
    c: Diameter(g12) = 4
    c: Distance(g-1,g10) = 172
    c: Distance(g-1,g9) = 127
    c: DistanceX(g7,g7) = 27
    c: DistanceY(g6,g6) = 19.5
    c: Diameter(g13) = 4
    c: Diameter(g14) = 4
    c: Diameter(g15) = 4
    c: Equal(g19, g20-g26) x7
    c: Diameter(g19) = 24
    c: Equal(g27,g26)
    c: DistanceY(g18) = 19.4093
    c: DistanceY(g17) = 13.0402
    c: DistanceY(g16) = -5.11795
    c: DistanceX(g19) = 37.5
    c: DistanceY(g19) = -22.3921
    c: DistanceY(g26) = 8.69222
    c: DistanceY(g27) = 39.4235
    c: Equal(g0,g1)
    c: Equal(g1,g2)
    c: Equal(g2,g3)
    c: Equal(g0,g16)
    c: Equal(g16,g17)
    c: Equal(g17,g18)
    c: Equal(g18,g27)
    c: DistanceY(g20) = 25.8987
    c: DistanceY(g22) = 31.4654
    c: DistanceY(g24) = -0.164634
    c: DistanceY(g25) = 1.52943
    c: DistanceY(g23) = 32.9074
    c: DistanceX(g18,g17) = 30.36
    c: DistanceX(g17,g16) = 25.22
    c: DistanceX(g-2,g16) = -37.5
    c: DistanceY(g21) = -5.58705
    c: DistanceX(g19,g21) = 26.56
    c: DistanceX(g26,g19) = 2.46
    c: DistanceX(g27,g19) = 3.82
    c: DistanceX(g19,g20) = 23.95
    c: DistanceX(g19,g24) = 57.43
    c: DistanceX(g19,g22) = 54.96
    c: DistanceX(g19,g25) = 88.7
    c: DistanceX(g19,g23) = 86.18
    c: DistanceY(g6,g15) = 14.25
    c: DistanceX(g6,g15) = 10.5
    c: DistanceY(g0,g14) = 24
    c: DistanceX(g14,g0) = 24
    c: Coincident(g28,g29)
    c: Coincident(g41,g30)
    c: Coincident(g30,g31)
    c: Coincident(g40,g28)
    c: Vertical(g28)
    c: Vertical(g30)
    c: Horizontal(g29)
    c: Horizontal(g31)
    c: Coincident(g32,g33)
    c: Coincident(g45,g34)
    c: Coincident(g34,g35)
    c: Coincident(g44,g32)
    c: Vertical(g32)
    c: Vertical(g34)
    c: Horizontal(g33)
    c: Horizontal(g35)
    c: Coincident(g36,g37)
    c: Coincident(g47,g38)
    c: Coincident(g38,g39)
    c: Coincident(g46,g36)
    c: Vertical(g36)
    c: Vertical(g38)
    c: Horizontal(g37)
    c: Horizontal(g39)
    c: DistanceX(g40,g31) = 26.5
    c: DistanceX(g44,g35) = 26.5
    c: DistanceX(g46,g39) = 26.5
    c: Distance(g18,g30) = 13.25
    c: Distance(g17,g34) = 13.25
    c: Distance(g16,g38) = 13.25
    c: DistanceY(g28,g28) = 4.5
    c: DistanceY(g32,g32) = 4.5
    c: DistanceY(g36,g36) = 4.5
    c: Distance(g18,g29) = 2.25
    c: Distance(g17,g33) = 2.25
    c: Distance(g16,g37) = 2.25
    c: PointOnObject(g42,g40)
    c: PointOnObject(g31,g42)
    c: PointOnObject(g40,g42)
    c: Coincident(g29,g18)
    c: Equal(g18,g42)
    c: Coincident(g18,g41)
    c: PointOnObject(g42,g31)
    c: Coincident(g18,g42)
    c: PointOnObject(g43,g44)
    c: Equal(g17,g43)
    c: PointOnObject(g17,g45)
    c: Coincident(g17,g43)
    c: Coincident(g35,g43)
    c: PointOnObject(g44,g43)
    c: Coincident(g33,g17)
    c: PointOnObject(g45,g17)
    c: PointOnObject(g39,g48)
    c: Coincident(g48,g46)
    c: Coincident(g16,g37)
    c: Equal(g16,g48)
    c: Coincident(g16,g47)
    c: PointOnObject(g48,g39)
    c: Coincident(g16,g48)
    c: Coincident(g49,g50)
    c: Coincident(g115,g51)
    c: Coincident(g51,g52)
    c: Coincident(g114,g49)
    c: Vertical(g49)
    c: Vertical(g51)
    c: Horizontal(g50)
    c: Horizontal(g52)
    c: Coincident(g53,g54)
    c: Coincident(g127,g55)
    c: Coincident(g55,g56)
    c: Coincident(g126,g53)
    c: Vertical(g53)
    c: Vertical(g55)
    c: Horizontal(g54)
    c: Horizontal(g56)
    c: Coincident(g57,g58)
    c: Coincident(g129,g59)
    c: Coincident(g59,g60)
    c: Coincident(g128,g57)
    c: Vertical(g57)
    c: Vertical(g59)
    c: Horizontal(g58)
    c: Horizontal(g60)
    c: Coincident(g61,g62)
    c: Coincident(g133,g63)
    c: Coincident(g63,g64)
    c: Coincident(g132,g61)
    c: Vertical(g61)
    c: Vertical(g63)
    c: Horizontal(g62)
    c: Horizontal(g64)
    c: Coincident(g65,g66)
    c: Coincident(g117,g67)
    c: Coincident(g67,g68)
    c: Coincident(g116,g65)
    c: Vertical(g65)
    c: Vertical(g67)
    c: Horizontal(g66)
    c: Horizontal(g68)
    c: Coincident(g69,g70)
    c: Coincident(g120,g71)
    c: Coincident(g71,g72)
    c: Coincident(g119,g69)
    c: Vertical(g69)
    c: Vertical(g71)
    c: Horizontal(g70)
    c: Horizontal(g72)
    c: Coincident(g73,g74)
    c: Coincident(g123,g75)
    c: Coincident(g75,g76)
    c: Coincident(g122,g73)
    c: Vertical(g73)
    c: Vertical(g75)
    c: Horizontal(g74)
    c: Horizontal(g76)
    c: Coincident(g77,g78)
    c: Coincident(g136,g79)
    c: Coincident(g79,g80)
    c: Coincident(g134,g77)
    c: Vertical(g77)
    c: Vertical(g79)
    c: Horizontal(g78)
    c: Horizontal(g80)
    c: Coincident(g81,g82)
    c: Coincident(g138,g83)
    c: Coincident(g83,g84)
    c: Coincident(g137,g81)
    c: Vertical(g81)
    c: Vertical(g83)
    c: Horizontal(g82)
    c: Horizontal(g84)
    c: Coincident(g85,g86)
    c: Coincident(g102,g87)
    c: Coincident(g87,g88)
    c: Coincident(g101,g85)
    c: Vertical(g85)
    c: Vertical(g87)
    c: Horizontal(g86)
    c: Horizontal(g88)
    c: Coincident(g89,g90)
    c: Coincident(g105,g91)
    c: Coincident(g91,g92)
    c: Coincident(g104,g89)
    c: Vertical(g89)
    c: Vertical(g91)
    c: Horizontal(g90)
    c: Horizontal(g92)
    c: Coincident(g93,g94)
    c: Coincident(g108,g95)
    c: Coincident(g95,g96)
    c: Coincident(g107,g93)
    c: Vertical(g93)
    c: Vertical(g95)
    c: Horizontal(g94)
    c: Horizontal(g96)
    c: Coincident(g97,g98)
    c: Coincident(g111,g99)
    c: Coincident(g99,g100)
    c: Coincident(g110,g97)
    c: Vertical(g97)
    c: Vertical(g99)
    c: Horizontal(g98)
    c: Horizontal(g100)
    c: DistanceX(g128,g60) = 26.5
    c: DistanceX(g126,g56) = 26.5
    c: DistanceX(g114,g52) = 26.5
    c: DistanceY(g85,g85) = 4.5
    c: Equal(g85,g89)
    c: Equal(g89,g93)
    c: Equal(g93,g97)
    c: Equal(g97,g49)
    c: Equal(g49,g53)
    c: Equal(g53,g57)
    c: Equal(g57,g61)
    c: Equal(g61,g65)
    c: Equal(g65,g69)
    c: Equal(g69,g77)
    c: Equal(g77,g73)
    c: Equal(g73,g81)
    c: Distance(g0,g88) = 2.25
    c: Distance(g1,g92) = 2.25
    c: Distance(g2,g96) = 2.25
    c: Distance(g3,g100) = 2.25
    c: Distance(g27,g52) = 2.25
    c: Distance(g26,g56) = 2.25
    c: Distance(g19,g60) = 2.25
    c: Distance(g21,g64) = 2.25
    c: Distance(g20,g68) = 2.25
    c: Distance(g22,g72) = 2.25
    c: Distance(g24,g80) = 2.25
    c: Distance(g23,g76) = 2.25
    c: Distance(g25,g84) = 2.25
    c: Distance(g0,g87) = 13.25
    c: DistanceX(g101,g88) = 26.5
    c: Distance(g1,g91) = 13.25
    c: Distance(g2,g95) = 13.25
    c: Distance(g3,g99) = 13.25
    c: Distance(g27,g51) = 13.25
    c: Distance(g26,g55) = 13.25
    c: Distance(g19,g59) = 13.25
    c: Distance(g20,g67) = 13.25
    c: Distance(g21,g63) = 13.25
    c: Distance(g24,g79) = 13.25
    c: Distance(g22,g71) = 13.25
    c: Distance(g23,g75) = 13.25
    c: Distance(g25,g83) = 13.25
    c: PointOnObject(g103,g101)
    c: PointOnObject(g88,g103)
    c: PointOnObject(g101,g103)
    c: Coincident(g86,g0)
    c: Equal(g0,g103)
    c: Coincident(g0,g102)
    c: PointOnObject(g103,g88)
    c: Coincident(g0,g103)
    c: PointOnObject(g106,g104)
    c: PointOnObject(g92,g106)
    c: PointOnObject(g104,g106)
    c: Coincident(g90,g1)
    c: Equal(g1,g106)
    c: Coincident(g1,g105)
    c: PointOnObject(g106,g92)
    c: Coincident(g1,g106)
    c: PointOnObject(g109,g107)
    c: PointOnObject(g96,g109)
    c: PointOnObject(g107,g109)
    c: Coincident(g94,g2)
    c: Equal(g2,g109)
    c: Coincident(g2,g108)
    c: PointOnObject(g109,g96)
    c: Coincident(g2,g109)
    c: PointOnObject(g112,g110)
    c: PointOnObject(g100,g112)
    c: PointOnObject(g110,g112)
    c: Coincident(g98,g3)
    c: Equal(g3,g112)
    c: Coincident(g3,g111)
    c: PointOnObject(g112,g100)
    c: Coincident(g3,g112)
    c: PointOnObject(g113,g114)
    c: Equal(g27,g113)
    c: PointOnObject(g27,g115)
    c: Coincident(g27,g113)
    c: Coincident(g52,g113)
    c: PointOnObject(g114,g113)
    c: Coincident(g50,g27)
    c: PointOnObject(g115,g27)
    c: PointOnObject(g118,g116)
    c: PointOnObject(g68,g118)
    c: PointOnObject(g116,g118)
    c: Coincident(g66,g20)
    c: Equal(g20,g118)
    c: Coincident(g20,g117)
    c: PointOnObject(g118,g68)
    c: Coincident(g20,g118)
    c: PointOnObject(g72,g121)
    c: Coincident(g121,g119)
    c: Coincident(g70,g22)
    c: Equal(g22,g121)
    c: Coincident(g22,g120)
    c: PointOnObject(g121,g72)
    c: Coincident(g22,g121)
    c: PointOnObject(g76,g124)
    c: Coincident(g124,g122)
    c: Coincident(g74,g23)
    c: Equal(g23,g124)
    c: Coincident(g23,g123)
    c: PointOnObject(g124,g76)
    c: Coincident(g23,g124)
    c: PointOnObject(g125,g127)
    c: Equal(g26,g125)
    c: PointOnObject(g26,g126)
    c: Coincident(g26,g125)
    c: Coincident(g56,g26)
    c: PointOnObject(g126,g26)
    c: Coincident(g54,g125)
    c: PointOnObject(g127,g125)
    c: PointOnObject(g130,g128)
    c: PointOnObject(g60,g130)
    c: PointOnObject(g128,g130)
    c: Coincident(g58,g19)
    c: Equal(g19,g130)
    c: Coincident(g19,g129)
    c: PointOnObject(g130,g60)
    c: Coincident(g19,g130)
    c: PointOnObject(g131,g132)
    c: Equal(g21,g131)
    c: PointOnObject(g21,g133)
    c: Coincident(g21,g131)
    c: Coincident(g64,g131)
    c: PointOnObject(g132,g131)
    c: Coincident(g62,g21)
    c: PointOnObject(g133,g21)
    c: PointOnObject(g135,g134)
    c: PointOnObject(g80,g135)
    c: PointOnObject(g134,g135)
    c: Equal(g24,g135)
    c: PointOnObject(g24,g136)
    c: PointOnObject(g135,g80)
    c: Coincident(g24,g135)
    c: Coincident(g78,g24)
    c: PointOnObject(g136,g24)
    c: PointOnObject(g139,g137)
    c: PointOnObject(g84,g139)
    c: PointOnObject(g137,g139)
    c: Coincident(g82,g25)
    c: Equal(g25,g139)
    c: Coincident(g25,g138)
    c: PointOnObject(g139,g84)
    c: Coincident(g25,g139)
    c: DistanceX(g141) = -31.49
    c: DistanceY(g141) = -60.3
    c: DistanceX(g140) = 28.44
    c: DistanceY(g140) = -60.3
    c: Diameter(g141) = 30
    c: Equal(g141,g140)
    c: Coincident(g142,g143)
    c: Coincident(g152,g144)
    c: Coincident(g144,g145)
    c: Coincident(g150,g142)
    c: Vertical(g142)
    c: Vertical(g144)
    c: Horizontal(g143)
    c: Horizontal(g145)
    c: Coincident(g146,g147)
    c: Coincident(g154,g148)
    c: Coincident(g148,g149)
    c: Coincident(g153,g146)
    c: Vertical(g146)
    c: Vertical(g148)
    c: Horizontal(g147)
    c: Horizontal(g149)
    c: DistanceX(g150,g145) = 32
    c: Distance(g141,g144) = 16
    c: Distance(g140,g148) = 16
    c: DistanceY(g142,g142) = 4.75
    c: Distance(g141,g143) = 2.375
    c: Distance(g140,g147) = 2.375
    c: Equal(g144,g146)
    c: PointOnObject(g151,g150)
    c: PointOnObject(g145,g151)
    c: PointOnObject(g150,g151)
    c: Equal(g141,g151)
    c: PointOnObject(g141,g152)
    c: PointOnObject(g151,g145)
    c: Coincident(g141,g151)
    c: Coincident(g143,g141)
    c: PointOnObject(g152,g141)
    c: PointOnObject(g155,g153)
    c: PointOnObject(g149,g155)
    c: PointOnObject(g153,g140)
    c: Coincident(g147,g140)
    c: Equal(g140,g155)
    c: Coincident(g140,g154)
    c: PointOnObject(g155,g149)
    c: Coincident(g140,g155)
FEATURE [Sketcher::SketchObject] Sketch003  label="Sketch12_5DegInwards"
  ArcFitTolerance = 1e-06
  AttachmentSupport = -> [XY_Plane]
  FullyConstrained = true
  MakeInternals = false
  MapMode = 5
  expr: Constraints[22] = Spreadsheet.BoxLength
  expr: Constraints[23] = Spreadsheet.BoxWidth
  expr: Constraints[35] = Spreadsheet.HolesEdgeStep
  expr: Constraints[36] = Spreadsheet.HolesEdgeStep
  expr: Constraints[37] = Spreadsheet.BoxLength / 2
  expr: Constraints[38] = Spreadsheet.BoxWidth / 2
  expr: Constraints[39] = Spreadsheet.OLEDLength
  expr: Constraints[40] = Spreadsheet.OLEDWidth
  expr: Constraints[44] = Spreadsheet.HolesEdgeStep
  expr: Constraints[47] = Spreadsheet.HolesEdgeStep
  expr: Constraints[48] = Spreadsheet.HolesEdgeStep
  expr: Constraints[54] = Spreadsheet.HolesEdgeStep
  expr: Constraints[55] = Spreadsheet.HolesEdgeStep
  sketch-geometry (38):
    g0: Circle CenterX=-128 CenterY=83 CenterZ=0 NormalX=0 NormalY=0 NormalZ=1 AngleXU=0 Radius=12
    g1: Circle CenterX=-95 CenterY=83 CenterZ=0 NormalX=0 NormalY=0 NormalZ=1 AngleXU=0 Radius=12
    g2: Circle CenterX=-62 CenterY=83 CenterZ=0 NormalX=0 NormalY=0 NormalZ=1 AngleXU=0 Radius=12
    g3: Circle CenterX=-29 CenterY=83 CenterZ=0 NormalX=0 NormalY=0 NormalZ=1 AngleXU=0 Radius=12
    g4: LineSegment StartX=114.5 StartY=92.75 StartZ=0 EndX=114.5 EndY=73.25 EndZ=0
    g5: LineSegment StartX=114.5 StartY=73.25 StartZ=0 EndX=141.5 EndY=73.25 EndZ=0
    g6: LineSegment StartX=141.5 StartY=73.25 StartZ=0 EndX=141.5 EndY=92.75 EndZ=0
    g7: LineSegment StartX=141.5 StartY=92.75 StartZ=0 EndX=114.5 EndY=92.75 EndZ=0
    g8: LineSegment StartX=-172 StartY=127 StartZ=0 EndX=-172 EndY=-127 EndZ=0
    g9: LineSegment StartX=-172 StartY=-127 StartZ=0 EndX=172 EndY=-127 EndZ=0
    g10: LineSegment StartX=172 StartY=-127 StartZ=0 EndX=172 EndY=127 EndZ=0
    g11: LineSegment StartX=172 StartY=127 StartZ=0 EndX=-172 EndY=127 EndZ=0
    g12: LineSegment StartX=-162 StartY=117 StartZ=0 EndX=-162 EndY=-117 EndZ=0
    g13: LineSegment StartX=-162 StartY=-117 StartZ=0 EndX=162 EndY=-117 EndZ=0
    g14: LineSegment StartX=162 StartY=-117 StartZ=0 EndX=162 EndY=117 EndZ=0
    g15: LineSegment StartX=162 StartY=117 StartZ=0 EndX=-162 EndY=117 EndZ=0
    g16: Circle CenterX=-152 CenterY=-107 CenterZ=0 NormalX=0 NormalY=0 NormalZ=1 AngleXU=0 Radius=2
    g17: Circle CenterX=152 CenterY=-107 CenterZ=0 NormalX=0 NormalY=0 NormalZ=1 AngleXU=0 Radius=2
    g18: Circle CenterX=152 CenterY=-107 CenterZ=0 NormalX=0 NormalY=0 NormalZ=1 AngleXU=0 Radius=1.5
    g19: Circle CenterX=-152 CenterY=107 CenterZ=0 NormalX=0 NormalY=0 NormalZ=1 AngleXU=0 Radius=2
    g20: Circle CenterX=-152 CenterY=107 CenterZ=0 NormalX=0 NormalY=0 NormalZ=1 AngleXU=0 Radius=1.5
    g21: Circle CenterX=152 CenterY=107 CenterZ=0 NormalX=0 NormalY=0 NormalZ=1 AngleXU=0 Radius=2
    g22: Circle CenterX=152 CenterY=107 CenterZ=0 NormalX=0 NormalY=0 NormalZ=1 AngleXU=0 Radius=1.5
    g23: Circle CenterX=-30 CenterY=-60.3 CenterZ=0 NormalX=0 NormalY=0 NormalZ=1 AngleXU=0 Radius=15
    g24: Circle CenterX=-33.59 CenterY=-4.91 CenterZ=0 NormalX=0 NormalY=0 NormalZ=1 AngleXU=0 Radius=12
    g25: Circle CenterX=-58.01 CenterY=14.33 CenterZ=0 NormalX=0 NormalY=0 NormalZ=1 AngleXU=0 Radius=12
    g26: Circle CenterX=-88.05 CenterY=22.02 CenterZ=0 NormalX=0 NormalY=0 NormalZ=1 AngleXU=0 Radius=12
    g27: Circle CenterX=30 CenterY=-60.3 CenterZ=0 NormalX=0 NormalY=0 NormalZ=1 AngleXU=0 Radius=15
    g28: Circle CenterX=37.39 CenterY=-22.03 CenterZ=0 NormalX=0 NormalY=0 NormalZ=1 AngleXU=0 Radius=12
    g29: Circle CenterX=59.21 CenterY=27.26 CenterZ=0 NormalX=0 NormalY=0 NormalZ=1 AngleXU=0 Radius=12
    g30: Circle CenterX=63.19 CenterY=-4.08 CenterZ=0 NormalX=0 NormalY=0 NormalZ=1 AngleXU=0 Radius=12
    g31: Circle CenterX=89.94 CenterY=34.17 CenterZ=0 NormalX=0 NormalY=0 NormalZ=1 AngleXU=0 Radius=12
    g32: Circle CenterX=121.07 CenterY=36.98 CenterZ=0 NormalX=0 NormalY=0 NormalZ=1 AngleXU=0 Radius=12
    g33: Circle CenterX=93.8 CenterY=2.68 CenterZ=0 NormalX=0 NormalY=0 NormalZ=1 AngleXU=0 Radius=12
    g34: Circle CenterX=124.97 CenterY=5.74 CenterZ=0 NormalX=0 NormalY=0 NormalZ=1 AngleXU=0 Radius=12
    g35: Circle CenterX=33.57 CenterY=8.91 CenterZ=0 NormalX=0 NormalY=0 NormalZ=1 AngleXU=0 Radius=12
    g36: Circle CenterX=30.88 CenterY=39.56 CenterZ=0 NormalX=0 NormalY=0 NormalZ=1 AngleXU=0 Radius=12
    g37: Circle CenterX=-152 CenterY=-107 CenterZ=0 NormalX=0 NormalY=0 NormalZ=1 AngleXU=0 Radius=1.5
  constraints (104):
    c: DistanceX(g0,g1) = 33
    c: DistanceX(g1,g2) = 33
    c: DistanceX(g2,g3) = 33
    c: Coincident(g4,g5)
    c: Coincident(g5,g6)
    c: Coincident(g6,g7)
    c: Coincident(g7,g4)
    c: Vertical(g4)
    c: Vertical(g6)
    c: Horizontal(g5)
    c: Horizontal(g7)
    c: Horizontal(g0,g1)
    c: Horizontal(g1,g2)
    c: Horizontal(g2,g3)
    c: Coincident(g8,g9)
    c: Coincident(g9,g10)
    c: Coincident(g10,g11)
    c: Coincident(g11,g8)
    c: Vertical(g8)
    c: Vertical(g10)
    c: Horizontal(g9)
    c: Horizontal(g11)
    c: DistanceX(g11,g11) = 344
    c: DistanceY(g8,g8) = 254
    c: Coincident(g12,g13)
    c: Coincident(g13,g14)
    c: Coincident(g14,g15)
    c: Coincident(g15,g12)
    c: Vertical(g12)
    c: Vertical(g14)
    c: Horizontal(g13)
    c: Horizontal(g15)
    c: DistanceY(g8,g12) = 10
    c: Distance(g12,g8) = 10
    c: Diameter(g16) = 4
    c: Distance(g16,g13) = 10
    c: Distance(g16,g12) = 10
    c: Distance(g-1,g10) = 172
    c: Distance(g-1,g9) = 127
    c: DistanceX(g7,g7) = 27
    c: DistanceY(g6,g6) = 19.5
    c: Diameter(g17) = 4
    c: Diameter(g18) = 3
    c: Coincident(g17,g18)
    c: Distance(g18,g13) = 10
    c: Diameter(g19) = 4
    c: Diameter(g20) = 3
    c: Distance(g19,g15) = 10
    c: Distance(g19,g12) = 10
    c: Distance(g13,g10) = 10
    c: Distance(g12,g11) = 10
    c: Diameter(g21) = 4
    c: Diameter(g22) = 3
    c: Coincident(g21,g22)
    c: Distance(g21,g15) = 10
    c: Distance(g21,g14) = 10
    c: DistanceY(g0,g19) = 24
    c: DistanceX(g19,g0) = 24
    c: DistanceX(g6,g21) = 10.5
    c: DistanceY(g6,g21) = 14.25
    c: Diameter(g23) = 30
    c: Equal(g28, g29-g35) x7
    c: Diameter(g28) = 24
    c: Equal(g36,g35)
    c: Distance(g23,g13) = 56.7
    c: DistanceX(g-2,g23) = -30
    c: DistanceX(g-2,g27) = 30
    c: Distance(g17,g14) = 10
    c: Distance(g27,g13) = 56.7
    c: Diameter(g27) = 30
    c: DistanceY(g23,g24) = 55.39
    c: DistanceX(g24,g23) = 3.59
    c: Diameter(g24) = 24
    c: Equal(g24,g25)
    c: Equal(g25,g26)
    c: DistanceY(g24,g25) = 19.24
    c: DistanceX(g25,g24) = 24.42
    c: DistanceY(g25,g26) = 7.69
    c: DistanceX(g26,g25) = 30.04
    c: DistanceY(g27,g28) = 38.27
    c: DistanceX(g27,g28) = 7.39
    c: DistanceY(g28,g35) = 30.94
    c: DistanceX(g35,g28) = 3.82
    c: DistanceY(g28,g30) = 17.95
    c: DistanceX(g28,g30) = 25.8
    c: DistanceY(g35,g36) = 30.65
    c: DistanceX(g36,g35) = 2.69
    c: Diameter(g0) = 24
    c: Equal(g0,g1)
    c: Equal(g1,g2)
    c: Equal(g2,g3)
    c: DistanceY(g35,g29) = 18.35
    c: DistanceX(g35,g29) = 25.64
    c: DistanceY(g30,g33) = 6.76
    c: DistanceX(g30,g33) = 30.61
    c: DistanceY(g29,g31) = 6.91
    c: DistanceX(g29,g31) = 30.73
    c: DistanceY(g33,g34) = 3.06
    c: DistanceX(g33,g34) = 31.17
    c: DistanceY(g31,g32) = 2.81
    c: DistanceX(g31,g32) = 31.13
    c: Coincident(g19,g20)
    c: Diameter(g37) = 3
    c: Coincident(g16,g37)
FEATURE [Sketcher::SketchObject] Sketch004  label="Sketch12_5DegInwardsWood"
  ArcFitTolerance = 1e-06
  AttachmentSupport = -> [XY_Plane]
  FullyConstrained = true
  MakeInternals = false
  MapMode = 5
  expr: Constraints[110] = Spreadsheet.Button24FlapWidth
  expr: Constraints[111] = Spreadsheet.Button24FlapLength
  expr: Constraints[22] = Spreadsheet.BoxLength
  expr: Constraints[23] = Spreadsheet.BoxWidth
  expr: Constraints[286] = Spreadsheet.Button30FlapLength
  expr: Constraints[287] = Spreadsheet.Button30FlapWidth
  expr: Constraints[35] = Spreadsheet.HolesEdgeStep
  expr: Constraints[36] = Spreadsheet.HolesEdgeStep
  expr: Constraints[37] = Spreadsheet.BoxLength / 2
  expr: Constraints[38] = Spreadsheet.BoxWidth / 2
  expr: Constraints[39] = Spreadsheet.OLEDLength
  expr: Constraints[40] = Spreadsheet.OLEDWidth
  expr: Constraints[43] = Spreadsheet.HolesEdgeStep
  expr: Constraints[44] = Spreadsheet.HolesEdgeStep
  expr: Constraints[48] = Spreadsheet.HolesEdgeStep
  expr: Constraints[49] = Spreadsheet.HolesEdgeStep
  sketch-geometry (106):
    g0: Circle CenterX=-128 CenterY=83 CenterZ=0 NormalX=0 NormalY=0 NormalZ=1 AngleXU=0 Radius=12
    g1: Circle CenterX=-95 CenterY=83 CenterZ=0 NormalX=0 NormalY=0 NormalZ=1 AngleXU=0 Radius=12
    g2: Circle CenterX=-62 CenterY=83 CenterZ=0 NormalX=0 NormalY=0 NormalZ=1 AngleXU=0 Radius=12
    g3: Circle CenterX=-29 CenterY=83 CenterZ=0 NormalX=0 NormalY=0 NormalZ=1 AngleXU=0 Radius=12
    g4: LineSegment StartX=114.5 StartY=92.75 StartZ=0 EndX=114.5 EndY=73.25 EndZ=0
    g5: LineSegment StartX=114.5 StartY=73.25 StartZ=0 EndX=141.5 EndY=73.25 EndZ=0
    g6: LineSegment StartX=141.5 StartY=73.25 StartZ=0 EndX=141.5 EndY=92.75 EndZ=0
    g7: LineSegment StartX=141.5 StartY=92.75 StartZ=0 EndX=114.5 EndY=92.75 EndZ=0
    g8: LineSegment StartX=-172 StartY=127 StartZ=0 EndX=-172 EndY=-127 EndZ=0
    g9: LineSegment StartX=-172 StartY=-127 StartZ=0 EndX=172 EndY=-127 EndZ=0
    g10: LineSegment StartX=172 StartY=-127 StartZ=0 EndX=172 EndY=127 EndZ=0
    g11: LineSegment StartX=172 StartY=127 StartZ=0 EndX=-172 EndY=127 EndZ=0
    g12: LineSegment StartX=-162 StartY=117 StartZ=0 EndX=-162 EndY=-117 EndZ=0
    g13: LineSegment StartX=-162 StartY=-117 StartZ=0 EndX=162 EndY=-117 EndZ=0
    g14: LineSegment StartX=162 StartY=-117 StartZ=0 EndX=162 EndY=117 EndZ=0
    g15: LineSegment StartX=162 StartY=117 StartZ=0 EndX=-162 EndY=117 EndZ=0
    g16: Circle CenterX=-152 CenterY=-107 CenterZ=0 NormalX=0 NormalY=0 NormalZ=1 AngleXU=0 Radius=2
    g17: Circle CenterX=152 CenterY=-107 CenterZ=0 NormalX=0 NormalY=0 NormalZ=1 AngleXU=0 Radius=2
    g18: Circle CenterX=-152 CenterY=107 CenterZ=0 NormalX=0 NormalY=0 NormalZ=1 AngleXU=0 Radius=2
    g19: Circle CenterX=152 CenterY=107 CenterZ=0 NormalX=0 NormalY=0 NormalZ=1 AngleXU=0 Radius=2
    g20: Circle CenterX=-30 CenterY=-60.3 CenterZ=0 NormalX=0 NormalY=0 NormalZ=1 AngleXU=0 Radius=15
    g21: Circle CenterX=-33.59 CenterY=-4.91 CenterZ=0 NormalX=0 NormalY=0 NormalZ=1 AngleXU=0 Radius=12
    g22: Circle CenterX=-58.01 CenterY=14.33 CenterZ=0 NormalX=0 NormalY=0 NormalZ=1 AngleXU=0 Radius=12
    g23: Circle CenterX=-88.05 CenterY=22.02 CenterZ=0 NormalX=0 NormalY=0 NormalZ=1 AngleXU=0 Radius=12
    g24: Circle CenterX=30 CenterY=-60.3 CenterZ=0 NormalX=0 NormalY=0 NormalZ=1 AngleXU=0 Radius=15
    g25: Circle CenterX=37.39 CenterY=-22.03 CenterZ=0 NormalX=0 NormalY=0 NormalZ=1 AngleXU=0 Radius=12
    g26: Circle CenterX=59.21 CenterY=27.26 CenterZ=0 NormalX=0 NormalY=0 NormalZ=1 AngleXU=0 Radius=12
    g27: Circle CenterX=63.19 CenterY=-4.08 CenterZ=0 NormalX=0 NormalY=0 NormalZ=1 AngleXU=0 Radius=12
    g28: Circle CenterX=89.94 CenterY=34.17 CenterZ=0 NormalX=0 NormalY=0 NormalZ=1 AngleXU=0 Radius=12
    g29: Circle CenterX=121.07 CenterY=36.98 CenterZ=0 NormalX=0 NormalY=0 NormalZ=1 AngleXU=0 Radius=12
    g30: Circle CenterX=93.8 CenterY=2.68 CenterZ=0 NormalX=0 NormalY=0 NormalZ=1 AngleXU=0 Radius=12
    g31: Circle CenterX=124.97 CenterY=5.74 CenterZ=0 NormalX=0 NormalY=0 NormalZ=1 AngleXU=0 Radius=12
    g32: Circle CenterX=33.57 CenterY=8.91 CenterZ=0 NormalX=0 NormalY=0 NormalZ=1 AngleXU=0 Radius=12
    g33: Circle CenterX=30.88 CenterY=39.56 CenterZ=0 NormalX=0 NormalY=0 NormalZ=1 AngleXU=0 Radius=12
    g34: LineSegment StartX=-42.25 StartY=85.25 StartZ=0 EndX=-42.25 EndY=80.75 EndZ=0
    g35: LineSegment StartX=-42.25 StartY=80.75 StartZ=0 EndX=-15.75 EndY=80.75 EndZ=0
    g36: LineSegment StartX=-15.75 StartY=80.75 StartZ=0 EndX=-15.75 EndY=85.25 EndZ=0
    g37: LineSegment StartX=-15.75 StartY=85.25 StartZ=0 EndX=-42.25 EndY=85.25 EndZ=0
    g38: LineSegment StartX=-141.25 StartY=85.25 StartZ=0 EndX=-141.25 EndY=80.75 EndZ=0
    g39: LineSegment StartX=-141.25 StartY=80.75 StartZ=0 EndX=-114.75 EndY=80.75 EndZ=0
    g40: LineSegment StartX=-114.75 StartY=80.75 StartZ=0 EndX=-114.75 EndY=85.25 EndZ=0
    g41: LineSegment StartX=-114.75 StartY=85.25 StartZ=0 EndX=-141.25 EndY=85.25 EndZ=0
    g42: LineSegment StartX=-108.25 StartY=85.25 StartZ=0 EndX=-108.25 EndY=80.75 EndZ=0
    g43: LineSegment StartX=-108.25 StartY=80.75 StartZ=0 EndX=-81.75 EndY=80.75 EndZ=0
    g44: LineSegment StartX=-81.75 StartY=80.75 StartZ=0 EndX=-81.75 EndY=85.25 EndZ=0
    g45: LineSegment StartX=-81.75 StartY=85.25 StartZ=0 EndX=-108.25 EndY=85.25 EndZ=0
    g46: LineSegment StartX=111.72 StartY=7.99 StartZ=0 EndX=111.72 EndY=3.49 EndZ=0
    g47: LineSegment StartX=111.72 StartY=3.49 StartZ=0 EndX=138.22 EndY=3.49 EndZ=0
    g48: LineSegment StartX=138.22 StartY=3.49 StartZ=0 EndX=138.22 EndY=7.99 EndZ=0
    g49: LineSegment StartX=138.22 StartY=7.99 StartZ=0 EndX=111.72 EndY=7.99 EndZ=0
    g50: LineSegment StartX=80.55 StartY=4.93 StartZ=0 EndX=80.55 EndY=0.43 EndZ=0
    g51: LineSegment StartX=80.55 StartY=0.43 StartZ=0 EndX=107.05 EndY=0.43 EndZ=0
    g52: LineSegment StartX=107.05 StartY=0.43 StartZ=0 EndX=107.05 EndY=4.93 EndZ=0
    g53: LineSegment StartX=107.05 StartY=4.93 StartZ=0 EndX=80.55 EndY=4.93 EndZ=0
    g54: LineSegment StartX=107.82 StartY=39.23 StartZ=0 EndX=107.82 EndY=34.73 EndZ=0
    g55: LineSegment StartX=107.82 StartY=34.73 StartZ=0 EndX=134.32 EndY=34.73 EndZ=0
    g56: LineSegment StartX=134.32 StartY=34.73 StartZ=0 EndX=134.32 EndY=39.23 EndZ=0
    g57: LineSegment StartX=134.32 StartY=39.23 StartZ=0 EndX=107.82 EndY=39.23 EndZ=0
    g58: LineSegment StartX=76.69 StartY=36.42 StartZ=0 EndX=76.69 EndY=31.92 EndZ=0
    g59: LineSegment StartX=76.69 StartY=31.92 StartZ=0 EndX=103.19 EndY=31.92 EndZ=0
    g60: LineSegment StartX=103.19 StartY=31.92 StartZ=0 EndX=103.19 EndY=36.42 EndZ=0
    g61: LineSegment StartX=103.19 StartY=36.42 StartZ=0 EndX=76.69 EndY=36.42 EndZ=0
    g62: LineSegment StartX=45.96 StartY=29.51 StartZ=0 EndX=45.96 EndY=25.01 EndZ=0
    g63: LineSegment StartX=45.96 StartY=25.01 StartZ=0 EndX=72.46 EndY=25.01 EndZ=0
    g64: LineSegment StartX=72.46 StartY=25.01 StartZ=0 EndX=72.46 EndY=29.51 EndZ=0
    g65: LineSegment StartX=72.46 StartY=29.51 StartZ=0 EndX=45.96 EndY=29.51 EndZ=0
    g66: LineSegment StartX=49.94 StartY=-1.83 StartZ=0 EndX=49.94 EndY=-6.33 EndZ=0
    g67: LineSegment StartX=49.94 StartY=-6.33 StartZ=0 EndX=76.44 EndY=-6.33 EndZ=0
    g68: LineSegment StartX=76.44 StartY=-6.33 StartZ=0 EndX=76.44 EndY=-1.83 EndZ=0
    g69: LineSegment StartX=76.44 StartY=-1.83 StartZ=0 EndX=49.94 EndY=-1.83 EndZ=0
    g70: LineSegment StartX=17.63 StartY=41.81 StartZ=0 EndX=17.63 EndY=37.31 EndZ=0
    g71: LineSegment StartX=17.63 StartY=37.31 StartZ=0 EndX=44.13 EndY=37.31 EndZ=0
    g72: LineSegment StartX=44.13 StartY=37.31 StartZ=0 EndX=44.13 EndY=41.81 EndZ=0
    g73: LineSegment StartX=44.13 StartY=41.81 StartZ=0 EndX=17.63 EndY=41.81 EndZ=0
    g74: LineSegment StartX=20.32 StartY=11.16 StartZ=0 EndX=20.32 EndY=6.66 EndZ=0
    g75: LineSegment StartX=20.32 StartY=6.66 StartZ=0 EndX=46.82 EndY=6.66 EndZ=0
    g76: LineSegment StartX=46.82 StartY=6.66 StartZ=0 EndX=46.82 EndY=11.16 EndZ=0
    g77: LineSegment StartX=46.82 StartY=11.16 StartZ=0 EndX=20.32 EndY=11.16 EndZ=0
    g78: LineSegment StartX=24.14 StartY=-19.78 StartZ=0 EndX=24.14 EndY=-24.28 EndZ=0
    g79: LineSegment StartX=24.14 StartY=-24.28 StartZ=0 EndX=50.64 EndY=-24.28 EndZ=0
    g80: LineSegment StartX=50.64 StartY=-24.28 StartZ=0 EndX=50.64 EndY=-19.78 EndZ=0
    g81: LineSegment StartX=50.64 StartY=-19.78 StartZ=0 EndX=24.14 EndY=-19.78 EndZ=0
    g82: LineSegment StartX=-46.84 StartY=-2.66 StartZ=0 EndX=-46.84 EndY=-7.16 EndZ=0
    g83: LineSegment StartX=-46.84 StartY=-7.16 StartZ=0 EndX=-20.34 EndY=-7.16 EndZ=0
    g84: LineSegment StartX=-20.34 StartY=-7.16 StartZ=0 EndX=-20.34 EndY=-2.66 EndZ=0
    g85: LineSegment StartX=-20.34 StartY=-2.66 StartZ=0 EndX=-46.84 EndY=-2.66 EndZ=0
    g86: LineSegment StartX=-71.26 StartY=16.58 StartZ=0 EndX=-71.26 EndY=12.08 EndZ=0
    g87: LineSegment StartX=-71.26 StartY=12.08 StartZ=0 EndX=-44.76 EndY=12.08 EndZ=0
    g88: LineSegment StartX=-44.76 StartY=12.08 StartZ=0 EndX=-44.76 EndY=16.58 EndZ=0
    g89: LineSegment StartX=-44.76 StartY=16.58 StartZ=0 EndX=-71.26 EndY=16.58 EndZ=0
    g90: LineSegment StartX=-101.3 StartY=24.27 StartZ=0 EndX=-101.3 EndY=19.77 EndZ=0
    g91: LineSegment StartX=-101.3 StartY=19.77 StartZ=0 EndX=-74.8 EndY=19.77 EndZ=0
    g92: LineSegment StartX=-74.8 StartY=19.77 StartZ=0 EndX=-74.8 EndY=24.27 EndZ=0
    g93: LineSegment StartX=-74.8 StartY=24.27 StartZ=0 EndX=-101.3 EndY=24.27 EndZ=0
    g94: LineSegment StartX=-75.25 StartY=85.25 StartZ=0 EndX=-75.25 EndY=80.75 EndZ=0
    g95: LineSegment StartX=-75.25 StartY=80.75 StartZ=0 EndX=-48.75 EndY=80.75 EndZ=0
    g96: LineSegment StartX=-48.75 StartY=80.75 StartZ=0 EndX=-48.75 EndY=85.25 EndZ=0
    g97: LineSegment StartX=-48.75 StartY=85.25 StartZ=0 EndX=-75.25 EndY=85.25 EndZ=0
    g98: LineSegment StartX=14 StartY=-57.925 StartZ=0 EndX=14 EndY=-62.675 EndZ=0
    g99: LineSegment StartX=14 StartY=-62.675 StartZ=0 EndX=46 EndY=-62.675 EndZ=0
    g100: LineSegment StartX=46 StartY=-62.675 StartZ=0 EndX=46 EndY=-57.925 EndZ=0
    g101: LineSegment StartX=46 StartY=-57.925 StartZ=0 EndX=14 EndY=-57.925 EndZ=0
    g102: LineSegment StartX=-46 StartY=-57.925 StartZ=0 EndX=-46 EndY=-62.675 EndZ=0
    g103: LineSegment StartX=-46 StartY=-62.675 StartZ=0 EndX=-14 EndY=-62.675 EndZ=0
    g104: LineSegment StartX=-14 StartY=-62.675 StartZ=0 EndX=-14 EndY=-57.925 EndZ=0
    g105: LineSegment StartX=-14 StartY=-57.925 StartZ=0 EndX=-46 EndY=-57.925 EndZ=0
  constraints (294):
    c: DistanceX(g0,g1) = 33
    c: DistanceX(g1,g2) = 33
    c: DistanceX(g2,g3) = 33
    c: Coincident(g4,g5)
    c: Coincident(g5,g6)
    c: Coincident(g6,g7)
    c: Coincident(g7,g4)
    c: Vertical(g4)
    c: Vertical(g6)
    c: Horizontal(g5)
    c: Horizontal(g7)
    c: Horizontal(g0,g1)
    c: Horizontal(g1,g2)
    c: Horizontal(g2,g3)
    c: Coincident(g8,g9)
    c: Coincident(g9,g10)
    c: Coincident(g10,g11)
    c: Coincident(g11,g8)
    c: Vertical(g8)
    c: Vertical(g10)
    c: Horizontal(g9)
    c: Horizontal(g11)
    c: DistanceX(g11,g11) = 344
    c: DistanceY(g8,g8) = 254
    c: Coincident(g12,g13)
    c: Coincident(g13,g14)
    c: Coincident(g14,g15)
    c: Coincident(g15,g12)
    c: Vertical(g12)
    c: Vertical(g14)
    c: Horizontal(g13)
    c: Horizontal(g15)
    c: DistanceY(g8,g12) = 10
    c: Distance(g12,g8) = 10
    c: Diameter(g16) = 4
    c: Distance(g16,g13) = 10
    c: Distance(g16,g12) = 10
    c: Distance(g-1,g10) = 172
    c: Distance(g-1,g9) = 127
    c: DistanceX(g7,g7) = 27
    c: DistanceY(g6,g6) = 19.5
    c: Diameter(g17) = 4
    c: Diameter(g18) = 4
    c: Distance(g18,g15) = 10
    c: Distance(g18,g12) = 10
    c: Distance(g13,g10) = 10
    c: Distance(g12,g11) = 10
    c: Diameter(g19) = 4
    c: Distance(g19,g15) = 10
    c: Distance(g19,g14) = 10
    c: DistanceY(g0,g18) = 24
    c: DistanceX(g18,g0) = 24
    c: DistanceX(g6,g19) = 10.5
    c: DistanceY(g6,g19) = 14.25
    c: Diameter(g20) = 30
    c: Equal(g25, g26-g32) x7
    c: Diameter(g25) = 24
    c: Equal(g33,g32)
    c: Distance(g20,g13) = 56.7
    c: DistanceX(g-2,g20) = -30
    c: DistanceX(g-2,g24) = 30
    c: Distance(g17,g14) = 10
    c: Distance(g24,g13) = 56.7
    c: Diameter(g24) = 30
    c: DistanceY(g20,g21) = 55.39
    c: DistanceX(g21,g20) = 3.59
    c: Diameter(g21) = 24
    c: Equal(g21,g22)
    c: Equal(g22,g23)
    c: DistanceY(g21,g22) = 19.24
    c: DistanceX(g22,g21) = 24.42
    c: DistanceY(g22,g23) = 7.69
    c: DistanceX(g23,g22) = 30.04
    c: DistanceY(g24,g25) = 38.27
    c: DistanceX(g24,g25) = 7.39
    c: DistanceY(g25,g32) = 30.94
    c: DistanceX(g32,g25) = 3.82
    c: DistanceY(g25,g27) = 17.95
    c: DistanceX(g25,g27) = 25.8
    c: DistanceY(g32,g33) = 30.65
    c: DistanceX(g33,g32) = 2.69
    c: Diameter(g0) = 24
    c: Equal(g0,g1)
    c: Equal(g1,g2)
    c: Equal(g2,g3)
    c: DistanceY(g32,g26) = 18.35
    c: DistanceX(g32,g26) = 25.64
    c: DistanceY(g27,g30) = 6.76
    c: DistanceX(g27,g30) = 30.61
    c: DistanceY(g26,g28) = 6.91
    c: DistanceX(g26,g28) = 30.73
    c: DistanceY(g30,g31) = 3.06
    c: DistanceX(g30,g31) = 31.17
    c: DistanceY(g28,g29) = 2.81
    c: DistanceX(g28,g29) = 31.13
    c: Distance(g17,g13) = 10
    c: Coincident(g34,g35)
    c: Coincident(g35,g36)
    c: Coincident(g36,g37)
    c: Coincident(g37,g34)
    c: Vertical(g34)
    c: Vertical(g36)
    c: Horizontal(g35)
    c: Horizontal(g37)
    c: DistanceY(g34,g34) = 4.5
    c: DistanceX(g37,g37) = 26.5
    c: Coincident(g38,g39)
    c: Coincident(g39,g40)
    c: Coincident(g40,g41)
    c: Coincident(g41,g38)
    c: Vertical(g38)
    c: Vertical(g40)
    c: Horizontal(g39)
    c: Horizontal(g41)
    c: DistanceY(g38,g38) = 4.5
    c: DistanceX(g41,g41) = 26.5
    c: Symmetric(g38,g40,g0)
    c: Coincident(g42,g43)
    c: Coincident(g43,g44)
    c: Coincident(g44,g45)
    c: Coincident(g45,g42)
    c: Vertical(g42)
    c: Vertical(g44)
    c: Horizontal(g43)
    c: Horizontal(g45)
    c: DistanceY(g42,g42) = 4.5
    c: DistanceX(g45,g45) = 26.5
    c: Coincident(g46,g47)
    c: Coincident(g47,g48)
    c: Coincident(g48,g49)
    c: Coincident(g49,g46)
    c: Vertical(g46)
    c: Vertical(g48)
    c: Horizontal(g47)
    c: Horizontal(g49)
    c: DistanceY(g46,g46) = 4.5
    c: DistanceX(g49,g49) = 26.5
    c: Coincident(g50,g51)
    c: Coincident(g51,g52)
    c: Coincident(g52,g53)
    c: Coincident(g53,g50)
    c: Vertical(g50)
    c: Vertical(g52)
    c: Horizontal(g51)
    c: Horizontal(g53)
    c: DistanceY(g50,g50) = 4.5
    c: DistanceX(g53,g53) = 26.5
    c: Coincident(g54,g55)
    c: Coincident(g55,g56)
    c: Coincident(g56,g57)
    c: Coincident(g57,g54)
    c: Vertical(g54)
    c: Vertical(g56)
    c: Horizontal(g55)
    c: Horizontal(g57)
    c: DistanceY(g54,g54) = 4.5
    c: DistanceX(g57,g57) = 26.5
    c: Coincident(g58,g59)
    c: Coincident(g59,g60)
    c: Coincident(g60,g61)
    c: Coincident(g61,g58)
    c: Vertical(g58)
    c: Vertical(g60)
    c: Horizontal(g59)
    c: Horizontal(g61)
    c: DistanceY(g58,g58) = 4.5
    c: DistanceX(g61,g61) = 26.5
    c: Symmetric(g46,g48,g31)
    c: Symmetric(g50,g52,g30)
    c: Symmetric(g58,g60,g28)
    c: Symmetric(g54,g56,g29)
    c: Coincident(g62,g63)
    c: Coincident(g63,g64)
    c: Coincident(g64,g65)
    c: Coincident(g65,g62)
    c: Vertical(g62)
    c: Vertical(g64)
    c: Horizontal(g63)
    c: Horizontal(g65)
    c: DistanceY(g62,g62) = 4.5
    c: DistanceX(g65,g65) = 26.5
    c: Coincident(g66,g67)
    c: Coincident(g67,g68)
    c: Coincident(g68,g69)
    c: Coincident(g69,g66)
    c: Vertical(g66)
    c: Vertical(g68)
    c: Horizontal(g67)
    c: Horizontal(g69)
    c: DistanceY(g66,g66) = 4.5
    c: DistanceX(g69,g69) = 26.5
    c: Coincident(g70,g71)
    c: Coincident(g71,g72)
    c: Coincident(g72,g73)
    c: Coincident(g73,g70)
    c: Vertical(g70)
    c: Vertical(g72)
    c: Horizontal(g71)
    c: Horizontal(g73)
    c: DistanceY(g70,g70) = 4.5
    c: DistanceX(g73,g73) = 26.5
    c: Coincident(g74,g75)
    c: Coincident(g75,g76)
    c: Coincident(g76,g77)
    c: Coincident(g77,g74)
    c: Vertical(g74)
    c: Vertical(g76)
    c: Horizontal(g75)
    c: Horizontal(g77)
    c: DistanceY(g74,g74) = 4.5
    c: DistanceX(g77,g77) = 26.5
    c: Coincident(g78,g79)
    c: Coincident(g79,g80)
    c: Coincident(g80,g81)
    c: Coincident(g81,g78)
    c: Vertical(g78)
    c: Vertical(g80)
    c: Horizontal(g79)
    c: Horizontal(g81)
    c: DistanceY(g78,g78) = 4.5
    c: DistanceX(g81,g81) = 26.5
    c: Symmetric(g70,g72,g33)
    c: Symmetric(g74,g76,g32)
    c: Symmetric(g66,g68,g27)
    c: Symmetric(g78,g80,g25)
    c: Symmetric(g62,g64,g26)
    c: Coincident(g82,g83)
    c: Coincident(g83,g84)
    c: Coincident(g84,g85)
    c: Coincident(g85,g82)
    c: Vertical(g82)
    c: Vertical(g84)
    c: Horizontal(g83)
    c: Horizontal(g85)
    c: DistanceY(g82,g82) = 4.5
    c: DistanceX(g85,g85) = 26.5
    c: Coincident(g86,g87)
    c: Coincident(g87,g88)
    c: Coincident(g88,g89)
    c: Coincident(g89,g86)
    c: Vertical(g86)
    c: Vertical(g88)
    c: Horizontal(g87)
    c: Horizontal(g89)
    c: DistanceY(g86,g86) = 4.5
    c: DistanceX(g89,g89) = 26.5
    c: Coincident(g90,g91)
    c: Coincident(g91,g92)
    c: Coincident(g92,g93)
    c: Coincident(g93,g90)
    c: Vertical(g90)
    c: Vertical(g92)
    c: Horizontal(g91)
    c: Horizontal(g93)
    c: DistanceY(g90,g90) = 4.5
    c: DistanceX(g93,g93) = 26.5
    c: Coincident(g94,g95)
    c: Coincident(g95,g96)
    c: Coincident(g96,g97)
    c: Coincident(g97,g94)
    c: Vertical(g94)
    c: Vertical(g96)
    c: Horizontal(g95)
    c: Horizontal(g97)
    c: DistanceY(g94,g94) = 4.5
    c: DistanceX(g97,g97) = 26.5
    c: Symmetric(g42,g44,g1)
    c: Symmetric(g94,g96,g2)
    c: Symmetric(g34,g36,g3)
    c: Symmetric(g90,g92,g23)
    c: Symmetric(g86,g88,g22)
    c: Symmetric(g82,g84,g21)
    c: Coincident(g98,g99)
    c: Coincident(g99,g100)
    c: Coincident(g100,g101)
    c: Coincident(g101,g98)
    c: Vertical(g98)
    c: Vertical(g100)
    c: Horizontal(g99)
    c: Horizontal(g101)
    c: DistanceX(g101,g101) = 32
    c: DistanceY(g98,g98) = 4.75
    c: Coincident(g102,g103)
    c: Coincident(g103,g104)
    c: Coincident(g104,g105)
    c: Coincident(g105,g102)
    c: Vertical(g102)
    c: Vertical(g104)
    c: Horizontal(g103)
    c: Horizontal(g105)
    c: DistanceX(g105,g105) = 32
    c: DistanceY(g102,g102) = 4.75
    c: Symmetric(g102,g104,g20)
    c: Symmetric(g98,g100,g24)
FEATURE [TechDraw::DrawSVGTemplate] Template
  Height = 297
  Orientation = 1
  Template = <path>
  Width = 420
FEATURE [TechDraw::DrawProjGroupItem] View
  CoarseView = false
  Direction = (0,0,1)
  Focus = 100
  HardHidden = false
  IsoCount = 0
  IsoHidden = false
  IsoVisible = false
  LockPosition = false
  Perspective = false
  Rotation = 0
  RotationVector = (1,0,0)
  ScaleType = 0
  ScrubCount = 1
  SeamHidden = false
  SeamVisible = false
  SmoothHidden = false
  SmoothVisible = true
  Source = -> [Sketch004]
  Type = 0
  X = 210
  XDirection = (1,0,0)
  Y = 148.5
FEATURE [TechDraw::DrawPage] Page  label="12_5DegInwardsWoodOutput"
  KeepUpdated = true
  NextBalloonIndex = 1
  ProjectionType = 0
  Template = -> Template
  Views = -> [View]
FEATURE [Sketcher::SketchObject] Sketch005  label="Sketch12_5DegInwardsAcrylic"
  ArcFitTolerance = 1e-06
  AttachmentSupport = -> [XY_Plane]
  FullyConstrained = true
  MakeInternals = false
  MapMode = 5
  expr: Constraints[14] = Spreadsheet.BoxLength
  expr: Constraints[15] = Spreadsheet.BoxWidth
  expr: Constraints[27] = Spreadsheet.HolesEdgeStep
  expr: Constraints[28] = Spreadsheet.HolesEdgeStep
  expr: Constraints[29] = Spreadsheet.BoxLength / 2
  expr: Constraints[30] = Spreadsheet.BoxWidth / 2
  expr: Constraints[33] = Spreadsheet.HolesEdgeStep
  expr: Constraints[34] = Spreadsheet.HolesEdgeStep
  expr: Constraints[38] = Spreadsheet.HolesEdgeStep
  expr: Constraints[39] = Spreadsheet.HolesEdgeStep
  sketch-geometry (30):
    g0: Circle CenterX=-128 CenterY=83 CenterZ=0 NormalX=0 NormalY=0 NormalZ=1 AngleXU=0 Radius=12
    g1: Circle CenterX=-95 CenterY=83 CenterZ=0 NormalX=0 NormalY=0 NormalZ=1 AngleXU=0 Radius=12
    g2: Circle CenterX=-62 CenterY=83 CenterZ=0 NormalX=0 NormalY=0 NormalZ=1 AngleXU=0 Radius=12
    g3: Circle CenterX=-29 CenterY=83 CenterZ=0 NormalX=0 NormalY=0 NormalZ=1 AngleXU=0 Radius=12
    g4: LineSegment StartX=-172 StartY=127 StartZ=0 EndX=-172 EndY=-127 EndZ=0
    g5: LineSegment StartX=-172 StartY=-127 StartZ=0 EndX=172 EndY=-127 EndZ=0
    g6: LineSegment StartX=172 StartY=-127 StartZ=0 EndX=172 EndY=127 EndZ=0
    g7: LineSegment StartX=172 StartY=127 StartZ=0 EndX=-172 EndY=127 EndZ=0
    g8: LineSegment StartX=-162 StartY=117 StartZ=0 EndX=-162 EndY=-117 EndZ=0
    g9: LineSegment StartX=-162 StartY=-117 StartZ=0 EndX=162 EndY=-117 EndZ=0
    g10: LineSegment StartX=162 StartY=-117 StartZ=0 EndX=162 EndY=117 EndZ=0
    g11: LineSegment StartX=162 StartY=117 StartZ=0 EndX=-162 EndY=117 EndZ=0
    g12: Circle CenterX=-152 CenterY=-107 CenterZ=0 NormalX=0 NormalY=0 NormalZ=1 AngleXU=0 Radius=2
    g13: Circle CenterX=152 CenterY=-107 CenterZ=0 NormalX=0 NormalY=0 NormalZ=1 AngleXU=0 Radius=2
    g14: Circle CenterX=-152 CenterY=107 CenterZ=0 NormalX=0 NormalY=0 NormalZ=1 AngleXU=0 Radius=2
    g15: Circle CenterX=152 CenterY=107 CenterZ=0 NormalX=0 NormalY=0 NormalZ=1 AngleXU=0 Radius=2
    g16: Circle CenterX=-30 CenterY=-60.3 CenterZ=0 NormalX=0 NormalY=0 NormalZ=1 AngleXU=0 Radius=15
    g17: Circle CenterX=-33.59 CenterY=-4.91 CenterZ=0 NormalX=0 NormalY=0 NormalZ=1 AngleXU=0 Radius=12
    g18: Circle CenterX=-58.01 CenterY=14.33 CenterZ=0 NormalX=0 NormalY=0 NormalZ=1 AngleXU=0 Radius=12
    g19: Circle CenterX=-88.05 CenterY=22.02 CenterZ=0 NormalX=0 NormalY=0 NormalZ=1 AngleXU=0 Radius=12
    g20: Circle CenterX=30 CenterY=-60.3 CenterZ=0 NormalX=0 NormalY=0 NormalZ=1 AngleXU=0 Radius=15
    g21: Circle CenterX=37.39 CenterY=-22.03 CenterZ=0 NormalX=0 NormalY=0 NormalZ=1 AngleXU=0 Radius=12
    g22: Circle CenterX=59.21 CenterY=27.26 CenterZ=0 NormalX=0 NormalY=0 NormalZ=1 AngleXU=0 Radius=12
    g23: Circle CenterX=63.19 CenterY=-4.08 CenterZ=0 NormalX=0 NormalY=0 NormalZ=1 AngleXU=0 Radius=12
    g24: Circle CenterX=89.94 CenterY=34.17 CenterZ=0 NormalX=0 NormalY=0 NormalZ=1 AngleXU=0 Radius=12
    g25: Circle CenterX=121.07 CenterY=36.98 CenterZ=0 NormalX=0 NormalY=0 NormalZ=1 AngleXU=0 Radius=12
    g26: Circle CenterX=93.8 CenterY=2.68 CenterZ=0 NormalX=0 NormalY=0 NormalZ=1 AngleXU=0 Radius=12
    g27: Circle CenterX=124.97 CenterY=5.74 CenterZ=0 NormalX=0 NormalY=0 NormalZ=1 AngleXU=0 Radius=12
    g28: Circle CenterX=33.57 CenterY=8.91 CenterZ=0 NormalX=0 NormalY=0 NormalZ=1 AngleXU=0 Radius=12
    g29: Circle CenterX=30.88 CenterY=39.56 CenterZ=0 NormalX=0 NormalY=0 NormalZ=1 AngleXU=0 Radius=12
  constraints (84):
    c: DistanceX(g0,g1) = 33
    c: DistanceX(g1,g2) = 33
    c: DistanceX(g2,g3) = 33
    c: Horizontal(g0,g1)
    c: Horizontal(g1,g2)
    c: Horizontal(g2,g3)
    c: Coincident(g4,g5)
    c: Coincident(g5,g6)
    c: Coincident(g6,g7)
    c: Coincident(g7,g4)
    c: Vertical(g4)
    c: Vertical(g6)
    c: Horizontal(g5)
    c: Horizontal(g7)
    c: DistanceX(g7,g7) = 344
    c: DistanceY(g4,g4) = 254
    c: Coincident(g8,g9)
    c: Coincident(g9,g10)
    c: Coincident(g10,g11)
    c: Coincident(g11,g8)
    c: Vertical(g8)
    c: Vertical(g10)
    c: Horizontal(g9)
    c: Horizontal(g11)
    c: DistanceY(g4,g8) = 10
    c: Distance(g8,g4) = 10
    c: Diameter(g12) = 4
    c: Distance(g12,g9) = 10
    c: Distance(g12,g8) = 10
    c: Distance(g-1,g6) = 172
    c: Distance(g-1,g5) = 127
    c: Diameter(g13) = 4
    c: Diameter(g14) = 4
    c: Distance(g14,g11) = 10
    c: Distance(g14,g8) = 10
    c: Distance(g9,g6) = 10
    c: Distance(g8,g7) = 10
    c: Diameter(g15) = 4
    c: Distance(g15,g11) = 10
    c: Distance(g15,g10) = 10
    c: DistanceY(g0,g14) = 24
    c: DistanceX(g14,g0) = 24
    c: Diameter(g16) = 30
    c: Equal(g21, g22-g28) x7
    c: Diameter(g21) = 24
    c: Equal(g29,g28)
    c: Distance(g16,g9) = 56.7
    c: DistanceX(g-2,g16) = -30
    c: DistanceX(g-2,g20) = 30
    c: Distance(g13,g10) = 10
    c: Distance(g20,g9) = 56.7
    c: Diameter(g20) = 30
    c: DistanceY(g16,g17) = 55.39
    c: DistanceX(g17,g16) = 3.59
    c: Diameter(g17) = 24
    c: Equal(g17,g18)
    c: Equal(g18,g19)
    c: DistanceY(g17,g18) = 19.24
    c: DistanceX(g18,g17) = 24.42
    c: DistanceY(g18,g19) = 7.69
    c: DistanceX(g19,g18) = 30.04
    c: DistanceY(g20,g21) = 38.27
    c: DistanceX(g20,g21) = 7.39
    c: DistanceY(g21,g28) = 30.94
    c: DistanceX(g28,g21) = 3.82
    c: DistanceY(g21,g23) = 17.95
    c: DistanceX(g21,g23) = 25.8
    c: DistanceY(g28,g29) = 30.65
    c: DistanceX(g29,g28) = 2.69
    c: Diameter(g0) = 24
    c: Equal(g0,g1)
    c: Equal(g1,g2)
    c: Equal(g2,g3)
    c: DistanceY(g28,g22) = 18.35
    c: DistanceX(g28,g22) = 25.64
    c: DistanceY(g23,g26) = 6.76
    c: DistanceX(g23,g26) = 30.61
    c: DistanceY(g22,g24) = 6.91
    c: DistanceX(g22,g24) = 30.73
    c: DistanceY(g26,g27) = 3.06
    c: DistanceX(g26,g27) = 31.17
    c: DistanceY(g24,g25) = 2.81
    c: DistanceX(g24,g25) = 31.13
    c: Distance(g13,g9) = 10
FEATURE [TechDraw::DrawSVGTemplate] Template001
  Height = 297
  Orientation = 1
  Template = <path>
  Width = 420
FEATURE [TechDraw::DrawProjGroupItem] View001
  CoarseView = false
  Direction = (0,0,1)
  Focus = 100
  HardHidden = false
  IsoCount = 0
  IsoHidden = false
  IsoVisible = false
  LockPosition = false
  Perspective = false
  Rotation = 0
  RotationVector = (1,0,0)
  ScaleType = 0
  ScrubCount = 1
  SeamHidden = false
  SeamVisible = false
  SmoothHidden = false
  SmoothVisible = true
  Source = -> [Sketch005]
  Type = 0
  X = 210
  XDirection = (1,0,0)
  Y = 148.5
FEATURE [TechDraw::DrawPage] Page001  label="12_5DegInwardsAcrylicOutput"
  KeepUpdated = true
  NextBalloonIndex = 1
  ProjectionType = 0
  Template = -> Template001
  Views = -> [View001]
FEATURE [Sketcher::SketchObject] Sketch006  label="Sketch12_5DegInwardsArtwork"
  ArcFitTolerance = 1e-06
  AttachmentSupport = -> [XY_Plane]
  FullyConstrained = true
  MakeInternals = false
  MapMode = 5
  expr: Constraints[22] = Spreadsheet.BoxLength
  expr: Constraints[23] = Spreadsheet.BoxWidth
  expr: Constraints[35] = Spreadsheet.HolesEdgeStep
  expr: Constraints[36] = Spreadsheet.HolesEdgeStep
  expr: Constraints[37] = Spreadsheet.BoxLength / 2
  expr: Constraints[38] = Spreadsheet.BoxWidth / 2
  expr: Constraints[39] = Spreadsheet.OLEDLength
  expr: Constraints[40] = Spreadsheet.OLEDWidth
  expr: Constraints[44] = Spreadsheet.HolesEdgeStep
  expr: Constraints[47] = Spreadsheet.HolesEdgeStep
  expr: Constraints[48] = Spreadsheet.HolesEdgeStep
  expr: Constraints[54] = Spreadsheet.HolesEdgeStep
  expr: Constraints[55] = Spreadsheet.HolesEdgeStep
  expr: Constraints[60] = Spreadsheet.Button30Outer
  expr: Constraints[68] = Spreadsheet.Button24Outer
  expr: Constraints[75] = Spreadsheet.Button30Outer
  expr: Constraints[78] = Spreadsheet.Button24Outer
  expr: Constraints[93] = Spreadsheet.Button24Outer
  sketch-geometry (38):
    g0: Circle CenterX=-128 CenterY=83 CenterZ=0 NormalX=0 NormalY=0 NormalZ=1 AngleXU=0 Radius=14
    g1: Circle CenterX=-95 CenterY=83 CenterZ=0 NormalX=0 NormalY=0 NormalZ=1 AngleXU=0 Radius=14
    g2: Circle CenterX=-62 CenterY=83 CenterZ=0 NormalX=0 NormalY=0 NormalZ=1 AngleXU=0 Radius=14
    g3: Circle CenterX=-29 CenterY=83 CenterZ=0 NormalX=0 NormalY=0 NormalZ=1 AngleXU=0 Radius=14
    g4: LineSegment StartX=114.5 StartY=92.75 StartZ=0 EndX=114.5 EndY=73.25 EndZ=0
    g5: LineSegment StartX=114.5 StartY=73.25 StartZ=0 EndX=141.5 EndY=73.25 EndZ=0
    g6: LineSegment StartX=141.5 StartY=73.25 StartZ=0 EndX=141.5 EndY=92.75 EndZ=0
    g7: LineSegment StartX=141.5 StartY=92.75 StartZ=0 EndX=114.5 EndY=92.75 EndZ=0
    g8: LineSegment StartX=-172 StartY=127 StartZ=0 EndX=-172 EndY=-127 EndZ=0
    g9: LineSegment StartX=-172 StartY=-127 StartZ=0 EndX=172 EndY=-127 EndZ=0
    g10: LineSegment StartX=172 StartY=-127 StartZ=0 EndX=172 EndY=127 EndZ=0
    g11: LineSegment StartX=172 StartY=127 StartZ=0 EndX=-172 EndY=127 EndZ=0
    g12: LineSegment StartX=-162 StartY=117 StartZ=0 EndX=-162 EndY=-117 EndZ=0
    g13: LineSegment StartX=-162 StartY=-117 StartZ=0 EndX=162 EndY=-117 EndZ=0
    g14: LineSegment StartX=162 StartY=-117 StartZ=0 EndX=162 EndY=117 EndZ=0
    g15: LineSegment StartX=162 StartY=117 StartZ=0 EndX=-162 EndY=117 EndZ=0
    g16: Circle CenterX=-152 CenterY=-107 CenterZ=0 NormalX=0 NormalY=0 NormalZ=1 AngleXU=0 Radius=2
    g17: Circle CenterX=152 CenterY=-107 CenterZ=0 NormalX=0 NormalY=0 NormalZ=1 AngleXU=0 Radius=2
    g18: Circle CenterX=152 CenterY=-107 CenterZ=0 NormalX=0 NormalY=0 NormalZ=1 AngleXU=0 Radius=1.5
    g19: Circle CenterX=-152 CenterY=107 CenterZ=0 NormalX=0 NormalY=0 NormalZ=1 AngleXU=0 Radius=2
    g20: Circle CenterX=-152 CenterY=107 CenterZ=0 NormalX=0 NormalY=0 NormalZ=1 AngleXU=0 Radius=1.5
    g21: Circle CenterX=152 CenterY=107 CenterZ=0 NormalX=0 NormalY=0 NormalZ=1 AngleXU=0 Radius=2
    g22: Circle CenterX=152 CenterY=107 CenterZ=0 NormalX=0 NormalY=0 NormalZ=1 AngleXU=0 Radius=1.5
    g23: Circle CenterX=-30 CenterY=-60.3 CenterZ=0 NormalX=0 NormalY=0 NormalZ=1 AngleXU=0 Radius=16.5
    g24: Circle CenterX=-33.59 CenterY=-4.91 CenterZ=0 NormalX=0 NormalY=0 NormalZ=1 AngleXU=0 Radius=14
    g25: Circle CenterX=-58.01 CenterY=14.33 CenterZ=0 NormalX=0 NormalY=0 NormalZ=1 AngleXU=0 Radius=14
    g26: Circle CenterX=-88.05 CenterY=22.02 CenterZ=0 NormalX=0 NormalY=0 NormalZ=1 AngleXU=0 Radius=14
    g27: Circle CenterX=30 CenterY=-60.3 CenterZ=0 NormalX=0 NormalY=0 NormalZ=1 AngleXU=0 Radius=16.5
    g28: Circle CenterX=37.39 CenterY=-22.03 CenterZ=0 NormalX=0 NormalY=0 NormalZ=1 AngleXU=0 Radius=14
    g29: Circle CenterX=59.21 CenterY=27.26 CenterZ=0 NormalX=0 NormalY=0 NormalZ=1 AngleXU=0 Radius=14
    g30: Circle CenterX=63.19 CenterY=-4.08 CenterZ=0 NormalX=0 NormalY=0 NormalZ=1 AngleXU=0 Radius=14
    g31: Circle CenterX=89.94 CenterY=34.17 CenterZ=0 NormalX=0 NormalY=0 NormalZ=1 AngleXU=0 Radius=14
    g32: Circle CenterX=121.07 CenterY=36.98 CenterZ=0 NormalX=0 NormalY=0 NormalZ=1 AngleXU=0 Radius=14
    g33: Circle CenterX=93.8 CenterY=2.68 CenterZ=0 NormalX=0 NormalY=0 NormalZ=1 AngleXU=0 Radius=14
    g34: Circle CenterX=124.97 CenterY=5.74 CenterZ=0 NormalX=0 NormalY=0 NormalZ=1 AngleXU=0 Radius=14
    g35: Circle CenterX=33.57 CenterY=8.91 CenterZ=0 NormalX=0 NormalY=0 NormalZ=1 AngleXU=0 Radius=14
    g36: Circle CenterX=30.88 CenterY=39.56 CenterZ=0 NormalX=0 NormalY=0 NormalZ=1 AngleXU=0 Radius=14
    g37: Circle CenterX=-152 CenterY=-107 CenterZ=0 NormalX=0 NormalY=0 NormalZ=1 AngleXU=0 Radius=1.5
  constraints (104):
    c: DistanceX(g0,g1) = 33
    c: DistanceX(g1,g2) = 33
    c: DistanceX(g2,g3) = 33
    c: Coincident(g4,g5)
    c: Coincident(g5,g6)
    c: Coincident(g6,g7)
    c: Coincident(g7,g4)
    c: Vertical(g4)
    c: Vertical(g6)
    c: Horizontal(g5)
    c: Horizontal(g7)
    c: Horizontal(g0,g1)
    c: Horizontal(g1,g2)
    c: Horizontal(g2,g3)
    c: Coincident(g8,g9)
    c: Coincident(g9,g10)
    c: Coincident(g10,g11)
    c: Coincident(g11,g8)
    c: Vertical(g8)
    c: Vertical(g10)
    c: Horizontal(g9)
    c: Horizontal(g11)
    c: DistanceX(g11,g11) = 344
    c: DistanceY(g8,g8) = 254
    c: Coincident(g12,g13)
    c: Coincident(g13,g14)
    c: Coincident(g14,g15)
    c: Coincident(g15,g12)
    c: Vertical(g12)
    c: Vertical(g14)
    c: Horizontal(g13)
    c: Horizontal(g15)
    c: DistanceY(g8,g12) = 10
    c: Distance(g12,g8) = 10
    c: Diameter(g16) = 4
    c: Distance(g16,g13) = 10
    c: Distance(g16,g12) = 10
    c: Distance(g-1,g10) = 172
    c: Distance(g-1,g9) = 127
    c: DistanceX(g7,g7) = 27
    c: DistanceY(g6,g6) = 19.5
    c: Diameter(g17) = 4
    c: Diameter(g18) = 3
    c: Coincident(g17,g18)
    c: Distance(g18,g13) = 10
    c: Diameter(g19) = 4
    c: Diameter(g20) = 3
    c: Distance(g19,g15) = 10
    c: Distance(g19,g12) = 10
    c: Distance(g13,g10) = 10
    c: Distance(g12,g11) = 10
    c: Diameter(g21) = 4
    c: Diameter(g22) = 3
    c: Coincident(g21,g22)
    c: Distance(g21,g15) = 10
    c: Distance(g21,g14) = 10
    c: DistanceY(g0,g19) = 24
    c: DistanceX(g19,g0) = 24
    c: DistanceX(g6,g21) = 10.5
    c: DistanceY(g6,g21) = 14.25
    c: Diameter(g23) = 33
    c: Equal(g28, g29-g35) x7
    c: Diameter(g28) = 28
    c: Equal(g36,g35)
    c: Distance(g23,g13) = 56.7
    c: DistanceX(g-2,g23) = -30
    c: DistanceX(g-2,g27) = 30
    c: Distance(g17,g14) = 10
    c: Distance(g27,g13) = 56.7
    c: Diameter(g27) = 33
    c: DistanceY(g23,g24) = 55.39
    c: DistanceX(g24,g23) = 3.59
    c: Diameter(g24) = 28
    c: Equal(g24,g25)
    c: Equal(g25,g26)
    c: DistanceY(g24,g25) = 19.24
    c: DistanceX(g25,g24) = 24.42
    c: DistanceY(g25,g26) = 7.69
    c: DistanceX(g26,g25) = 30.04
    c: DistanceY(g27,g28) = 38.27
    c: DistanceX(g27,g28) = 7.39
    c: DistanceY(g28,g35) = 30.94
    c: DistanceX(g35,g28) = 3.82
    c: DistanceY(g28,g30) = 17.95
    c: DistanceX(g28,g30) = 25.8
    c: DistanceY(g35,g36) = 30.65
    c: DistanceX(g36,g35) = 2.69
    c: Diameter(g0) = 28
    c: Equal(g0,g1)
    c: Equal(g1,g2)
    c: Equal(g2,g3)
    c: DistanceY(g35,g29) = 18.35
    c: DistanceX(g35,g29) = 25.64
    c: DistanceY(g30,g33) = 6.76
    c: DistanceX(g30,g33) = 30.61
    c: DistanceY(g29,g31) = 6.91
    c: DistanceX(g29,g31) = 30.73
    c: DistanceY(g33,g34) = 3.06
    c: DistanceX(g33,g34) = 31.17
    c: DistanceY(g31,g32) = 2.81
    c: DistanceX(g31,g32) = 31.13
    c: Coincident(g19,g20)
    c: Diameter(g37) = 3
    c: Coincident(g16,g37)
FEATURE [PartDesign::Body] Body
  AllowCompound = false
  Group = -> [Sketch,Sketch001,Sketch002,Sketch003,Sketch004,Sketch005,Sketch006]
  Origin = -> Origin
FEATURE [TechDraw::DrawSVGTemplate] Template002
  Height = 297
  Orientation = 1
  Template = <path>
  Width = 420
FEATURE [TechDraw::DrawProjGroupItem] View002
  CoarseView = false
  Direction = (0,0,1)
  Focus = 100
  HardHidden = false
  IsoCount = 0
  IsoHidden = false
  IsoVisible = false
  LockPosition = false
  Perspective = false
  Rotation = 0
  RotationVector = (1,0,0)
  ScaleType = 0
  ScrubCount = 1
  SeamHidden = false
  SeamVisible = false
  SmoothHidden = false
  SmoothVisible = true
  Source = -> [Sketch006]
  Type = 0
  X = 210
  XDirection = (1,0,0)
  Y = 148.5
FEATURE [TechDraw::DrawPage] Page002  label="12_5DegInwardsArtworkOutput"
  KeepUpdated = true
  NextBalloonIndex = 1
  ProjectionType = 0
  Template = -> Template002
  Views = -> [View002]
note: 3 file-system paths scrubbed to <path> (originals preserved in the JSON sidecar)
